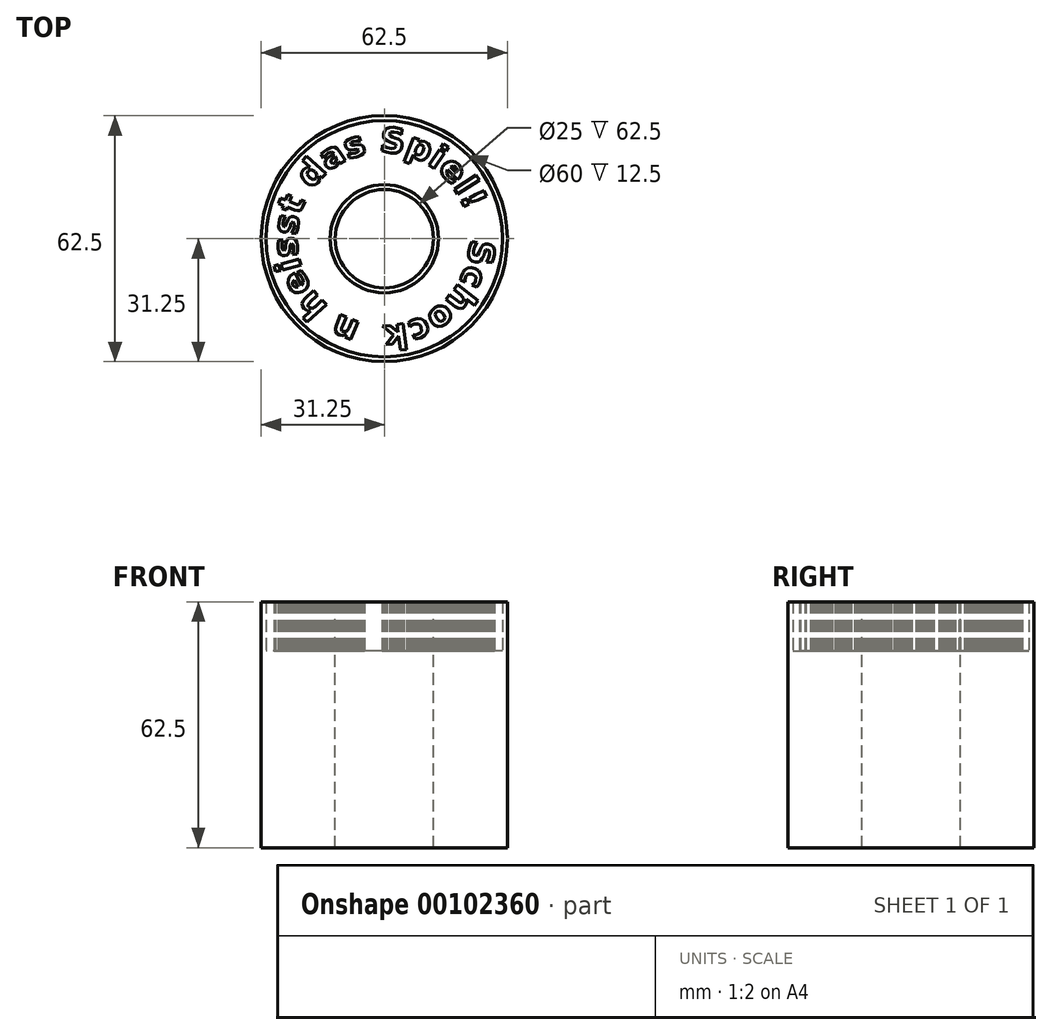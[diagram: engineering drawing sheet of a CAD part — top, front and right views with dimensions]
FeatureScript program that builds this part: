
annotation { "Feature Type Name" : "Feature", "Feature Type Description" : "" }
export const myFeature = defineFeature(function(context is Context, id is Id, definition is map)
    precondition{}
    {
        {
            var Q0;
            Q0=qCreatedBy(makeId("Top.planeOp"),FACE);
            var sketch = newSketch(context, id + "F0", { "sketchPlane" : qUnion([Q0])});
            skLineSegment(sketch, "E0", {"start": v(0.87, 0) * mm, "end": v(0.85, -0.18) * mm});
            skLineSegment(sketch, "E1", {"start": v(0.85, -0.18) * mm, "end": v(0.8, -0.34) * mm});
            skLineSegment(sketch, "E2", {"start": v(0.8, -0.34) * mm, "end": v(0.72, -0.5) * mm});
            skLineSegment(sketch, "E3", {"start": v(0.72, -0.5) * mm, "end": v(0.61, -0.62) * mm});
            skLineSegment(sketch, "E4", {"start": v(0.61, -0.62) * mm, "end": v(0.48, -0.73) * mm});
            skLineSegment(sketch, "E5", {"start": v(0.48, -0.73) * mm, "end": v(0.33, -0.81) * mm});
            skLineSegment(sketch, "E6", {"start": v(0.33, -0.81) * mm, "end": v(0.17, -0.86) * mm});
            skLineSegment(sketch, "E7", {"start": v(0.17, -0.86) * mm, "end": v(0, -0.88) * mm});
            skLineSegment(sketch, "E8", {"start": v(0, -0.88) * mm, "end": v(-0.19, -0.86) * mm});
            skLineSegment(sketch, "E9", {"start": v(-0.19, -0.86) * mm, "end": v(-0.35, -0.81) * mm});
            skLineSegment(sketch, "E10", {"start": v(-0.35, -0.81) * mm, "end": v(-0.5, -0.73) * mm});
            skLineSegment(sketch, "E11", {"start": v(-0.5, -0.73) * mm, "end": v(-0.63, -0.62) * mm});
            skLineSegment(sketch, "E12", {"start": v(-0.63, -0.62) * mm, "end": v(-0.74, -0.5) * mm});
            skLineSegment(sketch, "E13", {"start": v(-0.74, -0.5) * mm, "end": v(-0.82, -0.34) * mm});
            skLineSegment(sketch, "E14", {"start": v(-0.82, -0.34) * mm, "end": v(-0.87, -0.18) * mm});
            skLineSegment(sketch, "E15", {"start": v(-0.87, -0.18) * mm, "end": v(-0.89, 0) * mm});
            skLineSegment(sketch, "E16", {"start": v(-0.89, 0) * mm, "end": v(-0.87, 0.18) * mm});
            skLineSegment(sketch, "E17", {"start": v(-0.87, 0.18) * mm, "end": v(-0.82, 0.34) * mm});
            skLineSegment(sketch, "E18", {"start": v(-0.82, 0.34) * mm, "end": v(-0.74, 0.5) * mm});
            skLineSegment(sketch, "E19", {"start": v(-0.74, 0.5) * mm, "end": v(-0.63, 0.62) * mm});
            skLineSegment(sketch, "E20", {"start": v(-0.63, 0.62) * mm, "end": v(-0.5, 0.73) * mm});
            skLineSegment(sketch, "E21", {"start": v(-0.5, 0.73) * mm, "end": v(-0.35, 0.8) * mm});
            skLineSegment(sketch, "E22", {"start": v(-0.35, 0.8) * mm, "end": v(-0.19, 0.86) * mm});
            skLineSegment(sketch, "E23", {"start": v(-0.19, 0.86) * mm, "end": v(0, 0.88) * mm});
            skLineSegment(sketch, "E24", {"start": v(0, 0.88) * mm, "end": v(0.17, 0.86) * mm});
            skLineSegment(sketch, "E25", {"start": v(0.17, 0.86) * mm, "end": v(0.33, 0.8) * mm});
            skLineSegment(sketch, "E26", {"start": v(0.33, 0.8) * mm, "end": v(0.48, 0.73) * mm});
            skLineSegment(sketch, "E27", {"start": v(0.48, 0.73) * mm, "end": v(0.61, 0.62) * mm});
            skLineSegment(sketch, "E28", {"start": v(0.61, 0.62) * mm, "end": v(0.72, 0.5) * mm});
            skLineSegment(sketch, "E29", {"start": v(0.72, 0.5) * mm, "end": v(0.8, 0.34) * mm});
            skLineSegment(sketch, "E30", {"start": v(0.8, 0.34) * mm, "end": v(0.85, 0.18) * mm});
            skLineSegment(sketch, "E31", {"start": v(0.85, 0.18) * mm, "end": v(0.87, 0) * mm});
            skLineSegment(sketch, "E32", {"start": v(1.1, -0.24) * mm, "end": v(1.04, -0.24) * mm});
            skLineSegment(sketch, "E33", {"start": v(1.04, -0.24) * mm, "end": v(1.06, -0.2) * mm});
            skLineSegment(sketch, "E34", {"start": v(1.06, -0.2) * mm, "end": v(1.07, -0.16) * mm});
            skLineSegment(sketch, "E35", {"start": v(1.07, -0.16) * mm, "end": v(1.07, -0.13) * mm});
            skLineSegment(sketch, "E36", {"start": v(1.07, -0.13) * mm, "end": v(1.05, -0.11) * mm});
            skLineSegment(sketch, "E37", {"start": v(1.05, -0.11) * mm, "end": v(1.03, -0.12) * mm});
            skLineSegment(sketch, "E38", {"start": v(1.03, -0.12) * mm, "end": v(1.02, -0.14) * mm});
            skLineSegment(sketch, "E39", {"start": v(1.02, -0.14) * mm, "end": v(1.01, -0.17) * mm});
            skLineSegment(sketch, "E40", {"start": v(1.01, -0.17) * mm, "end": v(1, -0.2) * mm});
            skLineSegment(sketch, "E41", {"start": v(1, -0.2) * mm, "end": v(0.98, -0.23) * mm});
            skLineSegment(sketch, "E42", {"start": v(0.98, -0.23) * mm, "end": v(0.95, -0.24) * mm});
            skLineSegment(sketch, "E43", {"start": v(0.95, -0.24) * mm, "end": v(0.93, -0.24) * mm});
            skLineSegment(sketch, "E44", {"start": v(0.93, -0.24) * mm, "end": v(0.89, -0.22) * mm});
            skLineSegment(sketch, "E45", {"start": v(0.89, -0.22) * mm, "end": v(0.87, -0.2) * mm});
            skLineSegment(sketch, "E46", {"start": v(0.87, -0.2) * mm, "end": v(0.86, -0.17) * mm});
            skLineSegment(sketch, "E47", {"start": v(0.86, -0.17) * mm, "end": v(0.86, -0.12) * mm});
            skLineSegment(sketch, "E48", {"start": v(0.86, -0.12) * mm, "end": v(0.87, -0.08) * mm});
            skLineSegment(sketch, "E49", {"start": v(0.87, -0.08) * mm, "end": v(0.89, -0.03) * mm});
            skLineSegment(sketch, "E50", {"start": v(0.89, -0.03) * mm, "end": v(0.94, -0.04) * mm});
            skLineSegment(sketch, "E51", {"start": v(0.94, -0.04) * mm, "end": v(0.92, -0.08) * mm});
            skLineSegment(sketch, "E52", {"start": v(0.92, -0.08) * mm, "end": v(0.9, -0.12) * mm});
            skLineSegment(sketch, "E53", {"start": v(0.9, -0.12) * mm, "end": v(0.9, -0.16) * mm});
            skLineSegment(sketch, "E54", {"start": v(0.9, -0.16) * mm, "end": v(0.93, -0.17) * mm});
            skLineSegment(sketch, "E55", {"start": v(0.93, -0.17) * mm, "end": v(0.95, -0.17) * mm});
            skLineSegment(sketch, "E56", {"start": v(0.95, -0.17) * mm, "end": v(0.96, -0.14) * mm});
            skLineSegment(sketch, "E57", {"start": v(0.96, -0.14) * mm, "end": v(0.97, -0.11) * mm});
            skLineSegment(sketch, "E58", {"start": v(0.97, -0.11) * mm, "end": v(0.99, -0.08) * mm});
            skLineSegment(sketch, "E59", {"start": v(0.99, -0.08) * mm, "end": v(1, -0.06) * mm});
            skLineSegment(sketch, "E60", {"start": v(1, -0.06) * mm, "end": v(1.03, -0.05) * mm});
            skLineSegment(sketch, "E61", {"start": v(1.03, -0.05) * mm, "end": v(1.05, -0.05) * mm});
            skLineSegment(sketch, "E62", {"start": v(1.05, -0.05) * mm, "end": v(1.09, -0.06) * mm});
            skLineSegment(sketch, "E63", {"start": v(1.09, -0.06) * mm, "end": v(1.1, -0.08) * mm});
            skLineSegment(sketch, "E64", {"start": v(1.1, -0.08) * mm, "end": v(1.12, -0.12) * mm});
            skLineSegment(sketch, "E65", {"start": v(1.12, -0.12) * mm, "end": v(1.12, -0.16) * mm});
            skLineSegment(sketch, "E66", {"start": v(1.12, -0.16) * mm, "end": v(1.1, -0.2) * mm});
            skLineSegment(sketch, "E67", {"start": v(1.1, -0.2) * mm, "end": v(1.1, -0.24) * mm});
            skLineSegment(sketch, "E68", {"start": v(0.94, -0.5) * mm, "end": v(0.9, -0.47) * mm});
            skLineSegment(sketch, "E69", {"start": v(0.9, -0.47) * mm, "end": v(0.91, -0.45) * mm});
            skLineSegment(sketch, "E70", {"start": v(0.91, -0.45) * mm, "end": v(0.93, -0.43) * mm});
            skLineSegment(sketch, "E71", {"start": v(0.93, -0.43) * mm, "end": v(0.93, -0.39) * mm});
            skLineSegment(sketch, "E72", {"start": v(0.93, -0.39) * mm, "end": v(0.9, -0.36) * mm});
            skLineSegment(sketch, "E73", {"start": v(0.9, -0.36) * mm, "end": v(0.85, -0.36) * mm});
            skLineSegment(sketch, "E74", {"start": v(0.85, -0.36) * mm, "end": v(0.84, -0.37) * mm});
            skLineSegment(sketch, "E75", {"start": v(0.84, -0.37) * mm, "end": v(0.82, -0.39) * mm});
            skLineSegment(sketch, "E76", {"start": v(0.82, -0.39) * mm, "end": v(0.82, -0.41) * mm});
            skLineSegment(sketch, "E77", {"start": v(0.82, -0.41) * mm, "end": v(0.82, -0.44) * mm});
            skLineSegment(sketch, "E78", {"start": v(0.82, -0.44) * mm, "end": v(0.77, -0.42) * mm});
            skLineSegment(sketch, "E79", {"start": v(0.77, -0.42) * mm, "end": v(0.78, -0.4) * mm});
            skLineSegment(sketch, "E80", {"start": v(0.78, -0.4) * mm, "end": v(0.79, -0.36) * mm});
            skLineSegment(sketch, "E81", {"start": v(0.79, -0.36) * mm, "end": v(0.81, -0.32) * mm});
            skLineSegment(sketch, "E82", {"start": v(0.81, -0.32) * mm, "end": v(0.84, -0.3) * mm});
            skLineSegment(sketch, "E83", {"start": v(0.84, -0.3) * mm, "end": v(0.88, -0.3) * mm});
            skLineSegment(sketch, "E84", {"start": v(0.88, -0.3) * mm, "end": v(0.92, -0.3) * mm});
            skLineSegment(sketch, "E85", {"start": v(0.92, -0.3) * mm, "end": v(0.96, -0.33) * mm});
            skLineSegment(sketch, "E86", {"start": v(0.96, -0.33) * mm, "end": v(0.98, -0.36) * mm});
            skLineSegment(sketch, "E87", {"start": v(0.98, -0.36) * mm, "end": v(0.98, -0.4) * mm});
            skLineSegment(sketch, "E88", {"start": v(0.98, -0.4) * mm, "end": v(0.97, -0.44) * mm});
            skLineSegment(sketch, "E89", {"start": v(0.97, -0.44) * mm, "end": v(0.96, -0.47) * mm});
            skLineSegment(sketch, "E90", {"start": v(0.96, -0.47) * mm, "end": v(0.94, -0.5) * mm});
            skLineSegment(sketch, "E91", {"start": v(0.72, -0.69) * mm, "end": v(0.63, -0.62) * mm});
            skLineSegment(sketch, "E92", {"start": v(0.63, -0.62) * mm, "end": v(0.66, -0.57) * mm});
            skLineSegment(sketch, "E93", {"start": v(0.66, -0.57) * mm, "end": v(0.68, -0.58) * mm});
            skLineSegment(sketch, "E94", {"start": v(0.68, -0.58) * mm, "end": v(0.73, -0.62) * mm});
            skLineSegment(sketch, "E95", {"start": v(0.73, -0.62) * mm, "end": v(0.76, -0.64) * mm});
            skLineSegment(sketch, "E96", {"start": v(0.76, -0.64) * mm, "end": v(0.77, -0.65) * mm});
            skLineSegment(sketch, "E97", {"start": v(0.77, -0.65) * mm, "end": v(0.79, -0.65) * mm});
            skLineSegment(sketch, "E98", {"start": v(0.79, -0.65) * mm, "end": v(0.8, -0.64) * mm});
            skLineSegment(sketch, "E99", {"start": v(0.8, -0.64) * mm, "end": v(0.8, -0.6) * mm});
            skLineSegment(sketch, "E100", {"start": v(0.8, -0.6) * mm, "end": v(0.78, -0.57) * mm});
            skLineSegment(sketch, "E101", {"start": v(0.78, -0.57) * mm, "end": v(0.7, -0.51) * mm});
            skLineSegment(sketch, "E102", {"start": v(0.7, -0.51) * mm, "end": v(0.74, -0.47) * mm});
            skLineSegment(sketch, "E103", {"start": v(0.74, -0.47) * mm, "end": v(0.95, -0.63) * mm});
            skLineSegment(sketch, "E104", {"start": v(0.95, -0.63) * mm, "end": v(0.91, -0.68) * mm});
            skLineSegment(sketch, "E105", {"start": v(0.91, -0.68) * mm, "end": v(0.83, -0.62) * mm});
            skLineSegment(sketch, "E106", {"start": v(0.83, -0.62) * mm, "end": v(0.84, -0.65) * mm});
            skLineSegment(sketch, "E107", {"start": v(0.84, -0.65) * mm, "end": v(0.82, -0.69) * mm});
            skLineSegment(sketch, "E108", {"start": v(0.82, -0.69) * mm, "end": v(0.8, -0.7) * mm});
            skLineSegment(sketch, "E109", {"start": v(0.8, -0.7) * mm, "end": v(0.77, -0.71) * mm});
            skLineSegment(sketch, "E110", {"start": v(0.77, -0.71) * mm, "end": v(0.75, -0.7) * mm});
            skLineSegment(sketch, "E111", {"start": v(0.75, -0.7) * mm, "end": v(0.72, -0.69) * mm});
            skLineSegment(sketch, "E112", {"start": v(0.6, -0.83) * mm, "end": v(0.62, -0.8) * mm});
            skLineSegment(sketch, "E113", {"start": v(0.62, -0.8) * mm, "end": v(0.6, -0.76) * mm});
            skLineSegment(sketch, "E114", {"start": v(0.6, -0.76) * mm, "end": v(0.57, -0.74) * mm});
            skLineSegment(sketch, "E115", {"start": v(0.57, -0.74) * mm, "end": v(0.53, -0.74) * mm});
            skLineSegment(sketch, "E116", {"start": v(0.53, -0.74) * mm, "end": v(0.52, -0.77) * mm});
            skLineSegment(sketch, "E117", {"start": v(0.52, -0.77) * mm, "end": v(0.53, -0.81) * mm});
            skLineSegment(sketch, "E118", {"start": v(0.53, -0.81) * mm, "end": v(0.57, -0.84) * mm});
            skLineSegment(sketch, "E119", {"start": v(0.57, -0.84) * mm, "end": v(0.6, -0.83) * mm});
            skLineSegment(sketch, "E120", {"start": v(0.63, -0.87) * mm, "end": v(0.59, -0.89) * mm});
            skLineSegment(sketch, "E121", {"start": v(0.59, -0.89) * mm, "end": v(0.55, -0.9) * mm});
            skLineSegment(sketch, "E122", {"start": v(0.55, -0.9) * mm, "end": v(0.51, -0.88) * mm});
            skLineSegment(sketch, "E123", {"start": v(0.51, -0.88) * mm, "end": v(0.48, -0.85) * mm});
            skLineSegment(sketch, "E124", {"start": v(0.48, -0.85) * mm, "end": v(0.46, -0.81) * mm});
            skLineSegment(sketch, "E125", {"start": v(0.46, -0.81) * mm, "end": v(0.46, -0.77) * mm});
            skLineSegment(sketch, "E126", {"start": v(0.46, -0.77) * mm, "end": v(0.48, -0.74) * mm});
            skLineSegment(sketch, "E127", {"start": v(0.48, -0.74) * mm, "end": v(0.5, -0.7) * mm});
            skLineSegment(sketch, "E128", {"start": v(0.5, -0.7) * mm, "end": v(0.55, -0.69) * mm});
            skLineSegment(sketch, "E129", {"start": v(0.55, -0.69) * mm, "end": v(0.59, -0.68) * mm});
            skLineSegment(sketch, "E130", {"start": v(0.59, -0.68) * mm, "end": v(0.62, -0.7) * mm});
            skLineSegment(sketch, "E131", {"start": v(0.62, -0.7) * mm, "end": v(0.65, -0.73) * mm});
            skLineSegment(sketch, "E132", {"start": v(0.65, -0.73) * mm, "end": v(0.67, -0.76) * mm});
            skLineSegment(sketch, "E133", {"start": v(0.67, -0.76) * mm, "end": v(0.67, -0.8) * mm});
            skLineSegment(sketch, "E134", {"start": v(0.67, -0.8) * mm, "end": v(0.66, -0.84) * mm});
            skLineSegment(sketch, "E135", {"start": v(0.66, -0.84) * mm, "end": v(0.63, -0.87) * mm});
            skLineSegment(sketch, "E136", {"start": v(0.3, -1.02) * mm, "end": v(0.3, -0.97) * mm});
            skLineSegment(sketch, "E137", {"start": v(0.3, -0.97) * mm, "end": v(0.32, -0.98) * mm});
            skLineSegment(sketch, "E138", {"start": v(0.32, -0.98) * mm, "end": v(0.34, -0.97) * mm});
            skLineSegment(sketch, "E139", {"start": v(0.34, -0.97) * mm, "end": v(0.36, -0.96) * mm});
            skLineSegment(sketch, "E140", {"start": v(0.36, -0.96) * mm, "end": v(0.38, -0.94) * mm});
            skLineSegment(sketch, "E141", {"start": v(0.38, -0.94) * mm, "end": v(0.37, -0.9) * mm});
            skLineSegment(sketch, "E142", {"start": v(0.37, -0.9) * mm, "end": v(0.36, -0.88) * mm});
            skLineSegment(sketch, "E143", {"start": v(0.36, -0.88) * mm, "end": v(0.35, -0.86) * mm});
            skLineSegment(sketch, "E144", {"start": v(0.35, -0.86) * mm, "end": v(0.3, -0.87) * mm});
            skLineSegment(sketch, "E145", {"start": v(0.3, -0.87) * mm, "end": v(0.28, -0.88) * mm});
            skLineSegment(sketch, "E146", {"start": v(0.28, -0.88) * mm, "end": v(0.26, -0.9) * mm});
            skLineSegment(sketch, "E147", {"start": v(0.26, -0.9) * mm, "end": v(0.24, -0.85) * mm});
            skLineSegment(sketch, "E148", {"start": v(0.24, -0.85) * mm, "end": v(0.27, -0.84) * mm});
            skLineSegment(sketch, "E149", {"start": v(0.27, -0.84) * mm, "end": v(0.3, -0.82) * mm});
            skLineSegment(sketch, "E150", {"start": v(0.3, -0.82) * mm, "end": v(0.34, -0.81) * mm});
            skLineSegment(sketch, "E151", {"start": v(0.34, -0.81) * mm, "end": v(0.38, -0.82) * mm});
            skLineSegment(sketch, "E152", {"start": v(0.38, -0.82) * mm, "end": v(0.41, -0.84) * mm});
            skLineSegment(sketch, "E153", {"start": v(0.41, -0.84) * mm, "end": v(0.43, -0.87) * mm});
            skLineSegment(sketch, "E154", {"start": v(0.43, -0.87) * mm, "end": v(0.44, -0.92) * mm});
            skLineSegment(sketch, "E155", {"start": v(0.44, -0.92) * mm, "end": v(0.43, -0.95) * mm});
            skLineSegment(sketch, "E156", {"start": v(0.43, -0.95) * mm, "end": v(0.4, -0.99) * mm});
            skLineSegment(sketch, "E157", {"start": v(0.4, -0.99) * mm, "end": v(0.37, -1) * mm});
            skLineSegment(sketch, "E158", {"start": v(0.37, -1) * mm, "end": v(0.34, -1.02) * mm});
            skLineSegment(sketch, "E159", {"start": v(0.34, -1.02) * mm, "end": v(0.3, -1.02) * mm});
            skLineSegment(sketch, "E160", {"start": v(0.22, -1.12) * mm, "end": v(0.16, -1.13) * mm});
            skLineSegment(sketch, "E161", {"start": v(0.16, -1.13) * mm, "end": v(0.15, -0.99) * mm});
            skLineSegment(sketch, "E162", {"start": v(0.15, -0.99) * mm, "end": v(0.09, -1.07) * mm});
            skLineSegment(sketch, "E163", {"start": v(0.09, -1.07) * mm, "end": v(0.02, -1.08) * mm});
            skLineSegment(sketch, "E164", {"start": v(0.02, -1.08) * mm, "end": v(0.1, -0.98) * mm});
            skLineSegment(sketch, "E165", {"start": v(0.1, -0.98) * mm, "end": v(-0.02, -0.89) * mm});
            skLineSegment(sketch, "E166", {"start": v(-0.02, -0.89) * mm, "end": v(0.06, -0.88) * mm});
            skLineSegment(sketch, "E167", {"start": v(0.06, -0.88) * mm, "end": v(0.14, -0.95) * mm});
            skLineSegment(sketch, "E168", {"start": v(0.14, -0.95) * mm, "end": v(0.13, -0.87) * mm});
            skLineSegment(sketch, "E169", {"start": v(0.13, -0.87) * mm, "end": v(0.19, -0.86) * mm});
            skLineSegment(sketch, "E170", {"start": v(0.19, -0.86) * mm, "end": v(0.22, -1.12) * mm});
            skLineSegment(sketch, "E171", {"start": v(-0.23, -0.96) * mm, "end": v(-0.23, -0.94) * mm});
            skLineSegment(sketch, "E172", {"start": v(-0.23, -0.94) * mm, "end": v(-0.09, -0.96) * mm});
            skLineSegment(sketch, "E173", {"start": v(-0.09, -0.96) * mm, "end": v(-0.1, -0.92) * mm});
            skLineSegment(sketch, "E174", {"start": v(-0.1, -0.92) * mm, "end": v(-0.14, -0.9) * mm});
            skLineSegment(sketch, "E175", {"start": v(-0.14, -0.9) * mm, "end": v(-0.18, -0.9) * mm});
            skLineSegment(sketch, "E176", {"start": v(-0.18, -0.9) * mm, "end": v(-0.22, -0.92) * mm});
            skLineSegment(sketch, "E177", {"start": v(-0.22, -0.92) * mm, "end": v(-0.21, -0.87) * mm});
            skLineSegment(sketch, "E178", {"start": v(-0.21, -0.87) * mm, "end": v(-0.17, -0.87) * mm});
            skLineSegment(sketch, "E179", {"start": v(-0.17, -0.87) * mm, "end": v(-0.13, -0.87) * mm});
            skLineSegment(sketch, "E180", {"start": v(-0.13, -0.87) * mm, "end": v(-0.08, -0.88) * mm});
            skLineSegment(sketch, "E181", {"start": v(-0.08, -0.88) * mm, "end": v(-0.05, -0.9) * mm});
            skLineSegment(sketch, "E182", {"start": v(-0.05, -0.9) * mm, "end": v(-0.03, -0.94) * mm});
            skLineSegment(sketch, "E183", {"start": v(-0.03, -0.94) * mm, "end": v(-0.03, -0.98) * mm});
            skLineSegment(sketch, "E184", {"start": v(-0.03, -0.98) * mm, "end": v(-0.04, -1.02) * mm});
            skLineSegment(sketch, "E185", {"start": v(-0.04, -1.02) * mm, "end": v(-0.07, -1.05) * mm});
            skLineSegment(sketch, "E186", {"start": v(-0.07, -1.05) * mm, "end": v(-0.1, -1.07) * mm});
            skLineSegment(sketch, "E187", {"start": v(-0.1, -1.07) * mm, "end": v(-0.15, -1.07) * mm});
            skLineSegment(sketch, "E188", {"start": v(-0.15, -1.07) * mm, "end": v(-0.19, -1.06) * mm});
            skLineSegment(sketch, "E189", {"start": v(-0.19, -1.06) * mm, "end": v(-0.22, -1.03) * mm});
            skLineSegment(sketch, "E190", {"start": v(-0.14, -1) * mm, "end": v(-0.15, -0.96) * mm});
            skLineSegment(sketch, "E191", {"start": v(-0.23, -1) * mm, "end": v(-0.23, -0.96) * mm});
            skLineSegment(sketch, "E192", {"start": v(-0.17, -0.98) * mm, "end": v(-0.17, -1.01) * mm});
            skLineSegment(sketch, "E193", {"start": v(-0.17, -1.01) * mm, "end": v(-0.14, -1.03) * mm});
            skLineSegment(sketch, "E194", {"start": v(-0.14, -1.03) * mm, "end": v(-0.11, -1.02) * mm});
            skLineSegment(sketch, "E195", {"start": v(-0.11, -1.02) * mm, "end": v(-0.1, -1) * mm});
            skLineSegment(sketch, "E196", {"start": v(-0.1, -1) * mm, "end": v(-0.17, -0.98) * mm});
            skLineSegment(sketch, "E197", {"start": v(-0.49, -0.88) * mm, "end": v(-0.44, -0.77) * mm});
            skLineSegment(sketch, "E198", {"start": v(-0.44, -0.77) * mm, "end": v(-0.39, -0.8) * mm});
            skLineSegment(sketch, "E199", {"start": v(-0.39, -0.8) * mm, "end": v(-0.4, -0.81) * mm});
            skLineSegment(sketch, "E200", {"start": v(-0.4, -0.81) * mm, "end": v(-0.42, -0.88) * mm});
            skLineSegment(sketch, "E201", {"start": v(-0.42, -0.88) * mm, "end": v(-0.43, -0.91) * mm});
            skLineSegment(sketch, "E202", {"start": v(-0.43, -0.91) * mm, "end": v(-0.43, -0.92) * mm});
            skLineSegment(sketch, "E203", {"start": v(-0.43, -0.92) * mm, "end": v(-0.43, -0.94) * mm});
            skLineSegment(sketch, "E204", {"start": v(-0.43, -0.94) * mm, "end": v(-0.42, -0.95) * mm});
            skLineSegment(sketch, "E205", {"start": v(-0.42, -0.95) * mm, "end": v(-0.38, -0.94) * mm});
            skLineSegment(sketch, "E206", {"start": v(-0.38, -0.94) * mm, "end": v(-0.36, -0.91) * mm});
            skLineSegment(sketch, "E207", {"start": v(-0.36, -0.91) * mm, "end": v(-0.32, -0.82) * mm});
            skLineSegment(sketch, "E208", {"start": v(-0.32, -0.82) * mm, "end": v(-0.27, -0.85) * mm});
            skLineSegment(sketch, "E209", {"start": v(-0.27, -0.85) * mm, "end": v(-0.34, -1.02) * mm});
            skLineSegment(sketch, "E210", {"start": v(-0.34, -1.02) * mm, "end": v(-0.4, -1) * mm});
            skLineSegment(sketch, "E211", {"start": v(-0.4, -1) * mm, "end": v(-0.39, -0.97) * mm});
            skLineSegment(sketch, "E212", {"start": v(-0.39, -0.97) * mm, "end": v(-0.42, -0.98) * mm});
            skLineSegment(sketch, "E213", {"start": v(-0.42, -0.98) * mm, "end": v(-0.46, -0.98) * mm});
            skLineSegment(sketch, "E214", {"start": v(-0.46, -0.98) * mm, "end": v(-0.48, -0.96) * mm});
            skLineSegment(sketch, "E215", {"start": v(-0.48, -0.96) * mm, "end": v(-0.5, -0.94) * mm});
            skLineSegment(sketch, "E216", {"start": v(-0.5, -0.94) * mm, "end": v(-0.5, -0.91) * mm});
            skLineSegment(sketch, "E217", {"start": v(-0.5, -0.91) * mm, "end": v(-0.49, -0.88) * mm});
            skLineSegment(sketch, "E218", {"start": v(-0.8, -0.6) * mm, "end": v(-0.72, -0.53) * mm});
            skLineSegment(sketch, "E219", {"start": v(-0.72, -0.53) * mm, "end": v(-0.68, -0.57) * mm});
            skLineSegment(sketch, "E220", {"start": v(-0.68, -0.57) * mm, "end": v(-0.7, -0.59) * mm});
            skLineSegment(sketch, "E221", {"start": v(-0.7, -0.59) * mm, "end": v(-0.74, -0.63) * mm});
            skLineSegment(sketch, "E222", {"start": v(-0.74, -0.63) * mm, "end": v(-0.77, -0.66) * mm});
            skLineSegment(sketch, "E223", {"start": v(-0.77, -0.66) * mm, "end": v(-0.77, -0.67) * mm});
            skLineSegment(sketch, "E224", {"start": v(-0.77, -0.67) * mm, "end": v(-0.77, -0.68) * mm});
            skLineSegment(sketch, "E225", {"start": v(-0.77, -0.68) * mm, "end": v(-0.77, -0.7) * mm});
            skLineSegment(sketch, "E226", {"start": v(-0.77, -0.7) * mm, "end": v(-0.74, -0.7) * mm});
            skLineSegment(sketch, "E227", {"start": v(-0.74, -0.7) * mm, "end": v(-0.7, -0.69) * mm});
            skLineSegment(sketch, "E228", {"start": v(-0.7, -0.69) * mm, "end": v(-0.63, -0.62) * mm});
            skLineSegment(sketch, "E229", {"start": v(-0.63, -0.62) * mm, "end": v(-0.59, -0.67) * mm});
            skLineSegment(sketch, "E230", {"start": v(-0.59, -0.67) * mm, "end": v(-0.78, -0.85) * mm});
            skLineSegment(sketch, "E231", {"start": v(-0.78, -0.85) * mm, "end": v(-0.82, -0.8) * mm});
            skLineSegment(sketch, "E232", {"start": v(-0.82, -0.8) * mm, "end": v(-0.75, -0.73) * mm});
            skLineSegment(sketch, "E233", {"start": v(-0.75, -0.73) * mm, "end": v(-0.79, -0.73) * mm});
            skLineSegment(sketch, "E234", {"start": v(-0.79, -0.73) * mm, "end": v(-0.82, -0.71) * mm});
            skLineSegment(sketch, "E235", {"start": v(-0.82, -0.71) * mm, "end": v(-0.83, -0.69) * mm});
            skLineSegment(sketch, "E236", {"start": v(-0.83, -0.69) * mm, "end": v(-0.84, -0.66) * mm});
            skLineSegment(sketch, "E237", {"start": v(-0.84, -0.66) * mm, "end": v(-0.83, -0.63) * mm});
            skLineSegment(sketch, "E238", {"start": v(-0.83, -0.63) * mm, "end": v(-0.8, -0.6) * mm});
            skLineSegment(sketch, "E239", {"start": v(-0.92, -0.35) * mm, "end": v(-0.9, -0.35) * mm});
            skLineSegment(sketch, "E240", {"start": v(-0.9, -0.35) * mm, "end": v(-0.84, -0.47) * mm});
            skLineSegment(sketch, "E241", {"start": v(-0.84, -0.47) * mm, "end": v(-0.82, -0.45) * mm});
            skLineSegment(sketch, "E242", {"start": v(-0.82, -0.45) * mm, "end": v(-0.83, -0.4) * mm});
            skLineSegment(sketch, "E243", {"start": v(-0.83, -0.4) * mm, "end": v(-0.85, -0.37) * mm});
            skLineSegment(sketch, "E244", {"start": v(-0.85, -0.37) * mm, "end": v(-0.89, -0.35) * mm});
            skLineSegment(sketch, "E245", {"start": v(-0.89, -0.35) * mm, "end": v(-0.84, -0.32) * mm});
            skLineSegment(sketch, "E246", {"start": v(-0.84, -0.32) * mm, "end": v(-0.81, -0.36) * mm});
            skLineSegment(sketch, "E247", {"start": v(-0.81, -0.36) * mm, "end": v(-0.8, -0.4) * mm});
            skLineSegment(sketch, "E248", {"start": v(-0.8, -0.4) * mm, "end": v(-0.78, -0.44) * mm});
            skLineSegment(sketch, "E249", {"start": v(-0.78, -0.44) * mm, "end": v(-0.78, -0.48) * mm});
            skLineSegment(sketch, "E250", {"start": v(-0.78, -0.48) * mm, "end": v(-0.8, -0.51) * mm});
            skLineSegment(sketch, "E251", {"start": v(-0.8, -0.51) * mm, "end": v(-0.83, -0.54) * mm});
            skLineSegment(sketch, "E252", {"start": v(-0.83, -0.54) * mm, "end": v(-0.87, -0.55) * mm});
            skLineSegment(sketch, "E253", {"start": v(-0.87, -0.55) * mm, "end": v(-0.9, -0.55) * mm});
            skLineSegment(sketch, "E254", {"start": v(-0.9, -0.55) * mm, "end": v(-0.94, -0.52) * mm});
            skLineSegment(sketch, "E255", {"start": v(-0.94, -0.52) * mm, "end": v(-0.97, -0.49) * mm});
            skLineSegment(sketch, "E256", {"start": v(-0.97, -0.49) * mm, "end": v(-0.98, -0.45) * mm});
            skLineSegment(sketch, "E257", {"start": v(-0.98, -0.45) * mm, "end": v(-0.98, -0.41) * mm});
            skLineSegment(sketch, "E258", {"start": v(-0.98, -0.41) * mm, "end": v(-0.96, -0.38) * mm});
            skLineSegment(sketch, "E259", {"start": v(-0.96, -0.38) * mm, "end": v(-0.92, -0.35) * mm});
            skLineSegment(sketch, "E260", {"start": v(-0.91, -0.42) * mm, "end": v(-0.93, -0.44) * mm});
            skLineSegment(sketch, "E261", {"start": v(-0.93, -0.44) * mm, "end": v(-0.93, -0.47) * mm});
            skLineSegment(sketch, "E262", {"start": v(-0.93, -0.47) * mm, "end": v(-0.9, -0.5) * mm});
            skLineSegment(sketch, "E263", {"start": v(-0.9, -0.5) * mm, "end": v(-0.88, -0.5) * mm});
            skLineSegment(sketch, "E264", {"start": v(-0.88, -0.5) * mm, "end": v(-0.91, -0.42) * mm});
            skLineSegment(sketch, "E265", {"start": v(-1.03, -0.32) * mm, "end": v(-1.05, -0.26) * mm});
            skLineSegment(sketch, "E266", {"start": v(-1.05, -0.26) * mm, "end": v(-0.86, -0.2) * mm});
            skLineSegment(sketch, "E267", {"start": v(-0.86, -0.2) * mm, "end": v(-0.85, -0.27) * mm});
            skLineSegment(sketch, "E268", {"start": v(-0.85, -0.27) * mm, "end": v(-1.03, -0.32) * mm});
            skLineSegment(sketch, "E269", {"start": v(-1.1, -0.34) * mm, "end": v(-1.12, -0.28) * mm});
            skLineSegment(sketch, "E270", {"start": v(-1.12, -0.28) * mm, "end": v(-1.07, -0.26) * mm});
            skLineSegment(sketch, "E271", {"start": v(-1.07, -0.26) * mm, "end": v(-1.06, -0.32) * mm});
            skLineSegment(sketch, "E272", {"start": v(-1.06, -0.32) * mm, "end": v(-1.1, -0.34) * mm});
            skLineSegment(sketch, "E273", {"start": v(-1.08, -0.02) * mm, "end": v(-1.03, -0.01) * mm});
            skLineSegment(sketch, "E274", {"start": v(-1.03, -0.01) * mm, "end": v(-1.04, -0.05) * mm});
            skLineSegment(sketch, "E275", {"start": v(-1.04, -0.05) * mm, "end": v(-1.04, -0.09) * mm});
            skLineSegment(sketch, "E276", {"start": v(-1.04, -0.09) * mm, "end": v(-1.03, -0.11) * mm});
            skLineSegment(sketch, "E277", {"start": v(-1.03, -0.11) * mm, "end": v(-1.02, -0.12) * mm});
            skLineSegment(sketch, "E278", {"start": v(-1.02, -0.12) * mm, "end": v(-1, -0.11) * mm});
            skLineSegment(sketch, "E279", {"start": v(-1, -0.11) * mm, "end": v(-1, -0.09) * mm});
            skLineSegment(sketch, "E280", {"start": v(-1, -0.09) * mm, "end": v(-1, -0.08) * mm});
            skLineSegment(sketch, "E281", {"start": v(-1, -0.08) * mm, "end": v(-1, -0.04) * mm});
            skLineSegment(sketch, "E282", {"start": v(-1, -0.04) * mm, "end": v(-0.99, -0.01) * mm});
            skLineSegment(sketch, "E283", {"start": v(-0.99, -0.01) * mm, "end": v(-0.97, 0) * mm});
            skLineSegment(sketch, "E284", {"start": v(-0.97, 0) * mm, "end": v(-0.95, 0) * mm});
            skLineSegment(sketch, "E285", {"start": v(-0.95, 0) * mm, "end": v(-0.92, 0) * mm});
            skLineSegment(sketch, "E286", {"start": v(-0.92, 0) * mm, "end": v(-0.9, -0.01) * mm});
            skLineSegment(sketch, "E287", {"start": v(-0.9, -0.01) * mm, "end": v(-0.89, -0.04) * mm});
            skLineSegment(sketch, "E288", {"start": v(-0.89, -0.04) * mm, "end": v(-0.88, -0.08) * mm});
            skLineSegment(sketch, "E289", {"start": v(-0.88, -0.08) * mm, "end": v(-0.88, -0.12) * mm});
            skLineSegment(sketch, "E290", {"start": v(-0.88, -0.12) * mm, "end": v(-0.89, -0.16) * mm});
            skLineSegment(sketch, "E291", {"start": v(-0.89, -0.16) * mm, "end": v(-0.93, -0.16) * mm});
            skLineSegment(sketch, "E292", {"start": v(-0.93, -0.16) * mm, "end": v(-0.92, -0.12) * mm});
            skLineSegment(sketch, "E293", {"start": v(-0.92, -0.12) * mm, "end": v(-0.92, -0.08) * mm});
            skLineSegment(sketch, "E294", {"start": v(-0.92, -0.08) * mm, "end": v(-0.93, -0.06) * mm});
            skLineSegment(sketch, "E295", {"start": v(-0.93, -0.06) * mm, "end": v(-0.94, -0.05) * mm});
            skLineSegment(sketch, "E296", {"start": v(-0.94, -0.05) * mm, "end": v(-0.95, -0.06) * mm});
            skLineSegment(sketch, "E297", {"start": v(-0.95, -0.06) * mm, "end": v(-0.96, -0.08) * mm});
            skLineSegment(sketch, "E298", {"start": v(-0.96, -0.08) * mm, "end": v(-0.96, -0.1) * mm});
            skLineSegment(sketch, "E299", {"start": v(-0.96, -0.1) * mm, "end": v(-0.96, -0.13) * mm});
            skLineSegment(sketch, "E300", {"start": v(-0.96, -0.13) * mm, "end": v(-0.97, -0.15) * mm});
            skLineSegment(sketch, "E301", {"start": v(-0.97, -0.15) * mm, "end": v(-0.99, -0.17) * mm});
            skLineSegment(sketch, "E302", {"start": v(-0.99, -0.17) * mm, "end": v(-1.01, -0.17) * mm});
            skLineSegment(sketch, "E303", {"start": v(-1.01, -0.17) * mm, "end": v(-1.04, -0.17) * mm});
            skLineSegment(sketch, "E304", {"start": v(-1.04, -0.17) * mm, "end": v(-1.06, -0.15) * mm});
            skLineSegment(sketch, "E305", {"start": v(-1.06, -0.15) * mm, "end": v(-1.07, -0.13) * mm});
            skLineSegment(sketch, "E306", {"start": v(-1.07, -0.13) * mm, "end": v(-1.08, -0.1) * mm});
            skLineSegment(sketch, "E307", {"start": v(-1.08, -0.1) * mm, "end": v(-1.08, -0.06) * mm});
            skLineSegment(sketch, "E308", {"start": v(-1.08, -0.06) * mm, "end": v(-1.08, -0.02) * mm});
            skLineSegment(sketch, "E309", {"start": v(-1.05, 0.23) * mm, "end": v(-1, 0.23) * mm});
            skLineSegment(sketch, "E310", {"start": v(-1, 0.23) * mm, "end": v(-1.02, 0.2) * mm});
            skLineSegment(sketch, "E311", {"start": v(-1.02, 0.2) * mm, "end": v(-1.03, 0.16) * mm});
            skLineSegment(sketch, "E312", {"start": v(-1.03, 0.16) * mm, "end": v(-1.03, 0.13) * mm});
            skLineSegment(sketch, "E313", {"start": v(-1.03, 0.13) * mm, "end": v(-1.02, 0.12) * mm});
            skLineSegment(sketch, "E314", {"start": v(-1.02, 0.12) * mm, "end": v(-1, 0.13) * mm});
            skLineSegment(sketch, "E315", {"start": v(-1, 0.13) * mm, "end": v(-1, 0.15) * mm});
            skLineSegment(sketch, "E316", {"start": v(-1, 0.15) * mm, "end": v(-1, 0.16) * mm});
            skLineSegment(sketch, "E317", {"start": v(-1, 0.16) * mm, "end": v(-0.98, 0.2) * mm});
            skLineSegment(sketch, "E318", {"start": v(-0.98, 0.2) * mm, "end": v(-0.97, 0.22) * mm});
            skLineSegment(sketch, "E319", {"start": v(-0.97, 0.22) * mm, "end": v(-0.95, 0.23) * mm});
            skLineSegment(sketch, "E320", {"start": v(-0.95, 0.23) * mm, "end": v(-0.92, 0.23) * mm});
            skLineSegment(sketch, "E321", {"start": v(-0.92, 0.23) * mm, "end": v(-0.9, 0.22) * mm});
            skLineSegment(sketch, "E322", {"start": v(-0.9, 0.22) * mm, "end": v(-0.88, 0.2) * mm});
            skLineSegment(sketch, "E323", {"start": v(-0.88, 0.2) * mm, "end": v(-0.87, 0.17) * mm});
            skLineSegment(sketch, "E324", {"start": v(-0.87, 0.17) * mm, "end": v(-0.87, 0.13) * mm});
            skLineSegment(sketch, "E325", {"start": v(-0.87, 0.13) * mm, "end": v(-0.88, 0.1) * mm});
            skLineSegment(sketch, "E326", {"start": v(-0.88, 0.1) * mm, "end": v(-0.9, 0.05) * mm});
            skLineSegment(sketch, "E327", {"start": v(-0.9, 0.05) * mm, "end": v(-0.94, 0.06) * mm});
            skLineSegment(sketch, "E328", {"start": v(-0.94, 0.06) * mm, "end": v(-0.92, 0.1) * mm});
            skLineSegment(sketch, "E329", {"start": v(-0.92, 0.1) * mm, "end": v(-0.91, 0.13) * mm});
            skLineSegment(sketch, "E330", {"start": v(-0.91, 0.13) * mm, "end": v(-0.92, 0.16) * mm});
            skLineSegment(sketch, "E331", {"start": v(-0.92, 0.16) * mm, "end": v(-0.93, 0.17) * mm});
            skLineSegment(sketch, "E332", {"start": v(-0.93, 0.17) * mm, "end": v(-0.94, 0.16) * mm});
            skLineSegment(sketch, "E333", {"start": v(-0.94, 0.16) * mm, "end": v(-0.95, 0.14) * mm});
            skLineSegment(sketch, "E334", {"start": v(-0.95, 0.14) * mm, "end": v(-0.95, 0.13) * mm});
            skLineSegment(sketch, "E335", {"start": v(-0.95, 0.13) * mm, "end": v(-0.97, 0.1) * mm});
            skLineSegment(sketch, "E336", {"start": v(-0.97, 0.1) * mm, "end": v(-0.98, 0.08) * mm});
            skLineSegment(sketch, "E337", {"start": v(-0.98, 0.08) * mm, "end": v(-1, 0.07) * mm});
            skLineSegment(sketch, "E338", {"start": v(-1, 0.07) * mm, "end": v(-1.03, 0.07) * mm});
            skLineSegment(sketch, "E339", {"start": v(-1.03, 0.07) * mm, "end": v(-1.05, 0.08) * mm});
            skLineSegment(sketch, "E340", {"start": v(-1.05, 0.08) * mm, "end": v(-1.07, 0.1) * mm});
            skLineSegment(sketch, "E341", {"start": v(-1.07, 0.1) * mm, "end": v(-1.07, 0.12) * mm});
            skLineSegment(sketch, "E342", {"start": v(-1.07, 0.12) * mm, "end": v(-1.07, 0.16) * mm});
            skLineSegment(sketch, "E343", {"start": v(-1.07, 0.16) * mm, "end": v(-1.06, 0.2) * mm});
            skLineSegment(sketch, "E344", {"start": v(-1.06, 0.2) * mm, "end": v(-1.05, 0.23) * mm});
            skLineSegment(sketch, "E345", {"start": v(-1.05, 0.41) * mm, "end": v(-1, 0.4) * mm});
            skLineSegment(sketch, "E346", {"start": v(-1, 0.4) * mm, "end": v(-0.98, 0.45) * mm});
            skLineSegment(sketch, "E347", {"start": v(-0.98, 0.45) * mm, "end": v(-0.94, 0.44) * mm});
            skLineSegment(sketch, "E348", {"start": v(-0.94, 0.44) * mm, "end": v(-0.96, 0.38) * mm});
            skLineSegment(sketch, "E349", {"start": v(-0.96, 0.38) * mm, "end": v(-0.89, 0.35) * mm});
            skLineSegment(sketch, "E350", {"start": v(-0.89, 0.35) * mm, "end": v(-0.87, 0.35) * mm});
            skLineSegment(sketch, "E351", {"start": v(-0.87, 0.35) * mm, "end": v(-0.86, 0.36) * mm});
            skLineSegment(sketch, "E352", {"start": v(-0.86, 0.36) * mm, "end": v(-0.85, 0.4) * mm});
            skLineSegment(sketch, "E353", {"start": v(-0.85, 0.4) * mm, "end": v(-0.8, 0.38) * mm});
            skLineSegment(sketch, "E354", {"start": v(-0.8, 0.38) * mm, "end": v(-0.82, 0.33) * mm});
            skLineSegment(sketch, "E355", {"start": v(-0.82, 0.33) * mm, "end": v(-0.84, 0.3) * mm});
            skLineSegment(sketch, "E356", {"start": v(-0.84, 0.3) * mm, "end": v(-0.86, 0.29) * mm});
            skLineSegment(sketch, "E357", {"start": v(-0.86, 0.29) * mm, "end": v(-0.88, 0.28) * mm});
            skLineSegment(sketch, "E358", {"start": v(-0.88, 0.28) * mm, "end": v(-0.9, 0.3) * mm});
            skLineSegment(sketch, "E359", {"start": v(-0.9, 0.3) * mm, "end": v(-0.99, 0.32) * mm});
            skLineSegment(sketch, "E360", {"start": v(-0.99, 0.32) * mm, "end": v(-1, 0.3) * mm});
            skLineSegment(sketch, "E361", {"start": v(-1, 0.3) * mm, "end": v(-1.04, 0.3) * mm});
            skLineSegment(sketch, "E362", {"start": v(-1.04, 0.3) * mm, "end": v(-1.03, 0.34) * mm});
            skLineSegment(sketch, "E363", {"start": v(-1.03, 0.34) * mm, "end": v(-1.08, 0.35) * mm});
            skLineSegment(sketch, "E364", {"start": v(-1.08, 0.35) * mm, "end": v(-1.05, 0.41) * mm});
            skLineSegment(sketch, "E365", {"start": v(-0.76, 0.73) * mm, "end": v(-0.83, 0.8) * mm});
            skLineSegment(sketch, "E366", {"start": v(-0.83, 0.8) * mm, "end": v(-0.79, 0.84) * mm});
            skLineSegment(sketch, "E367", {"start": v(-0.79, 0.84) * mm, "end": v(-0.6, 0.66) * mm});
            skLineSegment(sketch, "E368", {"start": v(-0.6, 0.66) * mm, "end": v(-0.64, 0.62) * mm});
            skLineSegment(sketch, "E369", {"start": v(-0.64, 0.62) * mm, "end": v(-0.66, 0.64) * mm});
            skLineSegment(sketch, "E370", {"start": v(-0.66, 0.64) * mm, "end": v(-0.66, 0.6) * mm});
            skLineSegment(sketch, "E371", {"start": v(-0.66, 0.6) * mm, "end": v(-0.67, 0.57) * mm});
            skLineSegment(sketch, "E372", {"start": v(-0.67, 0.57) * mm, "end": v(-0.7, 0.55) * mm});
            skLineSegment(sketch, "E373", {"start": v(-0.7, 0.55) * mm, "end": v(-0.73, 0.54) * mm});
            skLineSegment(sketch, "E374", {"start": v(-0.73, 0.54) * mm, "end": v(-0.77, 0.55) * mm});
            skLineSegment(sketch, "E375", {"start": v(-0.77, 0.55) * mm, "end": v(-0.8, 0.57) * mm});
            skLineSegment(sketch, "E376", {"start": v(-0.8, 0.57) * mm, "end": v(-0.83, 0.6) * mm});
            skLineSegment(sketch, "E377", {"start": v(-0.83, 0.6) * mm, "end": v(-0.84, 0.64) * mm});
            skLineSegment(sketch, "E378", {"start": v(-0.84, 0.64) * mm, "end": v(-0.84, 0.67) * mm});
            skLineSegment(sketch, "E379", {"start": v(-0.84, 0.67) * mm, "end": v(-0.82, 0.7) * mm});
            skLineSegment(sketch, "E380", {"start": v(-0.82, 0.7) * mm, "end": v(-0.8, 0.72) * mm});
            skLineSegment(sketch, "E381", {"start": v(-0.8, 0.72) * mm, "end": v(-0.76, 0.73) * mm});
            skLineSegment(sketch, "E382", {"start": v(-0.7, 0.61) * mm, "end": v(-0.68, 0.65) * mm});
            skLineSegment(sketch, "E383", {"start": v(-0.68, 0.65) * mm, "end": v(-0.7, 0.68) * mm});
            skLineSegment(sketch, "E384", {"start": v(-0.7, 0.68) * mm, "end": v(-0.74, 0.7) * mm});
            skLineSegment(sketch, "E385", {"start": v(-0.74, 0.7) * mm, "end": v(-0.77, 0.69) * mm});
            skLineSegment(sketch, "E386", {"start": v(-0.77, 0.69) * mm, "end": v(-0.78, 0.66) * mm});
            skLineSegment(sketch, "E387", {"start": v(-0.78, 0.66) * mm, "end": v(-0.76, 0.62) * mm});
            skLineSegment(sketch, "E388", {"start": v(-0.76, 0.62) * mm, "end": v(-0.72, 0.6) * mm});
            skLineSegment(sketch, "E389", {"start": v(-0.72, 0.6) * mm, "end": v(-0.7, 0.61) * mm});
            skLineSegment(sketch, "E390", {"start": v(-0.52, 0.82) * mm, "end": v(-0.54, 0.8) * mm});
            skLineSegment(sketch, "E391", {"start": v(-0.54, 0.8) * mm, "end": v(-0.54, 0.78) * mm});
            skLineSegment(sketch, "E392", {"start": v(-0.54, 0.78) * mm, "end": v(-0.52, 0.76) * mm});
            skLineSegment(sketch, "E393", {"start": v(-0.52, 0.76) * mm, "end": v(-0.5, 0.77) * mm});
            skLineSegment(sketch, "E394", {"start": v(-0.5, 0.77) * mm, "end": v(-0.48, 0.8) * mm});
            skLineSegment(sketch, "E395", {"start": v(-0.48, 0.8) * mm, "end": v(-0.49, 0.83) * mm});
            skLineSegment(sketch, "E396", {"start": v(-0.49, 0.83) * mm, "end": v(-0.5, 0.83) * mm});
            skLineSegment(sketch, "E397", {"start": v(-0.5, 0.83) * mm, "end": v(-0.52, 0.82) * mm});
            skLineSegment(sketch, "E398", {"start": v(-0.45, 0.89) * mm, "end": v(-0.4, 0.8) * mm});
            skLineSegment(sketch, "E399", {"start": v(-0.4, 0.8) * mm, "end": v(-0.45, 0.76) * mm});
            skLineSegment(sketch, "E400", {"start": v(-0.45, 0.76) * mm, "end": v(-0.46, 0.79) * mm});
            skLineSegment(sketch, "E401", {"start": v(-0.46, 0.79) * mm, "end": v(-0.47, 0.75) * mm});
            skLineSegment(sketch, "E402", {"start": v(-0.47, 0.75) * mm, "end": v(-0.5, 0.72) * mm});
            skLineSegment(sketch, "E403", {"start": v(-0.5, 0.72) * mm, "end": v(-0.55, 0.71) * mm});
            skLineSegment(sketch, "E404", {"start": v(-0.55, 0.71) * mm, "end": v(-0.57, 0.72) * mm});
            skLineSegment(sketch, "E405", {"start": v(-0.57, 0.72) * mm, "end": v(-0.6, 0.74) * mm});
            skLineSegment(sketch, "E406", {"start": v(-0.6, 0.74) * mm, "end": v(-0.6, 0.77) * mm});
            skLineSegment(sketch, "E407", {"start": v(-0.6, 0.77) * mm, "end": v(-0.6, 0.8) * mm});
            skLineSegment(sketch, "E408", {"start": v(-0.6, 0.8) * mm, "end": v(-0.58, 0.82) * mm});
            skLineSegment(sketch, "E409", {"start": v(-0.58, 0.82) * mm, "end": v(-0.54, 0.85) * mm});
            skLineSegment(sketch, "E410", {"start": v(-0.54, 0.85) * mm, "end": v(-0.51, 0.87) * mm});
            skLineSegment(sketch, "E411", {"start": v(-0.51, 0.87) * mm, "end": v(-0.52, 0.87) * mm});
            skLineSegment(sketch, "E412", {"start": v(-0.52, 0.87) * mm, "end": v(-0.54, 0.88) * mm});
            skLineSegment(sketch, "E413", {"start": v(-0.54, 0.88) * mm, "end": v(-0.57, 0.87) * mm});
            skLineSegment(sketch, "E414", {"start": v(-0.57, 0.87) * mm, "end": v(-0.6, 0.85) * mm});
            skLineSegment(sketch, "E415", {"start": v(-0.6, 0.85) * mm, "end": v(-0.62, 0.82) * mm});
            skLineSegment(sketch, "E416", {"start": v(-0.62, 0.82) * mm, "end": v(-0.64, 0.86) * mm});
            skLineSegment(sketch, "E417", {"start": v(-0.64, 0.86) * mm, "end": v(-0.61, 0.89) * mm});
            skLineSegment(sketch, "E418", {"start": v(-0.61, 0.89) * mm, "end": v(-0.58, 0.9) * mm});
            skLineSegment(sketch, "E419", {"start": v(-0.58, 0.9) * mm, "end": v(-0.54, 0.93) * mm});
            skLineSegment(sketch, "E420", {"start": v(-0.54, 0.93) * mm, "end": v(-0.5, 0.93) * mm});
            skLineSegment(sketch, "E421", {"start": v(-0.5, 0.93) * mm, "end": v(-0.48, 0.92) * mm});
            skLineSegment(sketch, "E422", {"start": v(-0.48, 0.92) * mm, "end": v(-0.45, 0.89) * mm});
            skLineSegment(sketch, "E423", {"start": v(-0.26, 1.04) * mm, "end": v(-0.24, 1) * mm});
            skLineSegment(sketch, "E424", {"start": v(-0.24, 1) * mm, "end": v(-0.28, 1) * mm});
            skLineSegment(sketch, "E425", {"start": v(-0.28, 1) * mm, "end": v(-0.32, 0.99) * mm});
            skLineSegment(sketch, "E426", {"start": v(-0.32, 0.99) * mm, "end": v(-0.34, 0.97) * mm});
            skLineSegment(sketch, "E427", {"start": v(-0.34, 0.97) * mm, "end": v(-0.34, 0.96) * mm});
            skLineSegment(sketch, "E428", {"start": v(-0.34, 0.96) * mm, "end": v(-0.33, 0.95) * mm});
            skLineSegment(sketch, "E429", {"start": v(-0.33, 0.95) * mm, "end": v(-0.31, 0.95) * mm});
            skLineSegment(sketch, "E430", {"start": v(-0.31, 0.95) * mm, "end": v(-0.3, 0.95) * mm});
            skLineSegment(sketch, "E431", {"start": v(-0.3, 0.95) * mm, "end": v(-0.26, 0.96) * mm});
            skLineSegment(sketch, "E432", {"start": v(-0.26, 0.96) * mm, "end": v(-0.23, 0.95) * mm});
            skLineSegment(sketch, "E433", {"start": v(-0.23, 0.95) * mm, "end": v(-0.22, 0.94) * mm});
            skLineSegment(sketch, "E434", {"start": v(-0.22, 0.94) * mm, "end": v(-0.2, 0.92) * mm});
            skLineSegment(sketch, "E435", {"start": v(-0.2, 0.92) * mm, "end": v(-0.2, 0.9) * mm});
            skLineSegment(sketch, "E436", {"start": v(-0.2, 0.9) * mm, "end": v(-0.21, 0.87) * mm});
            skLineSegment(sketch, "E437", {"start": v(-0.21, 0.87) * mm, "end": v(-0.24, 0.85) * mm});
            skLineSegment(sketch, "E438", {"start": v(-0.24, 0.85) * mm, "end": v(-0.27, 0.83) * mm});
            skLineSegment(sketch, "E439", {"start": v(-0.27, 0.83) * mm, "end": v(-0.31, 0.82) * mm});
            skLineSegment(sketch, "E440", {"start": v(-0.31, 0.82) * mm, "end": v(-0.35, 0.82) * mm});
            skLineSegment(sketch, "E441", {"start": v(-0.35, 0.82) * mm, "end": v(-0.37, 0.86) * mm});
            skLineSegment(sketch, "E442", {"start": v(-0.37, 0.86) * mm, "end": v(-0.33, 0.86) * mm});
            skLineSegment(sketch, "E443", {"start": v(-0.33, 0.86) * mm, "end": v(-0.29, 0.87) * mm});
            skLineSegment(sketch, "E444", {"start": v(-0.29, 0.87) * mm, "end": v(-0.26, 0.88) * mm});
            skLineSegment(sketch, "E445", {"start": v(-0.26, 0.88) * mm, "end": v(-0.26, 0.9) * mm});
            skLineSegment(sketch, "E446", {"start": v(-0.26, 0.9) * mm, "end": v(-0.27, 0.9) * mm});
            skLineSegment(sketch, "E447", {"start": v(-0.27, 0.9) * mm, "end": v(-0.3, 0.9) * mm});
            skLineSegment(sketch, "E448", {"start": v(-0.3, 0.9) * mm, "end": v(-0.3, 0.9) * mm});
            skLineSegment(sketch, "E449", {"start": v(-0.3, 0.9) * mm, "end": v(-0.34, 0.9) * mm});
            skLineSegment(sketch, "E450", {"start": v(-0.34, 0.9) * mm, "end": v(-0.37, 0.9) * mm});
            skLineSegment(sketch, "E451", {"start": v(-0.37, 0.9) * mm, "end": v(-0.38, 0.92) * mm});
            skLineSegment(sketch, "E452", {"start": v(-0.38, 0.92) * mm, "end": v(-0.4, 0.94) * mm});
            skLineSegment(sketch, "E453", {"start": v(-0.4, 0.94) * mm, "end": v(-0.4, 0.97) * mm});
            skLineSegment(sketch, "E454", {"start": v(-0.4, 0.97) * mm, "end": v(-0.39, 1) * mm});
            skLineSegment(sketch, "E455", {"start": v(-0.39, 1) * mm, "end": v(-0.37, 1) * mm});
            skLineSegment(sketch, "E456", {"start": v(-0.37, 1) * mm, "end": v(-0.33, 1.02) * mm});
            skLineSegment(sketch, "E457", {"start": v(-0.33, 1.02) * mm, "end": v(-0.3, 1.03) * mm});
            skLineSegment(sketch, "E458", {"start": v(-0.3, 1.03) * mm, "end": v(-0.26, 1.04) * mm});
            skLineSegment(sketch, "E459", {"start": v(0.18, 1.11) * mm, "end": v(0.18, 1.06) * mm});
            skLineSegment(sketch, "E460", {"start": v(0.18, 1.06) * mm, "end": v(0.14, 1.08) * mm});
            skLineSegment(sketch, "E461", {"start": v(0.14, 1.08) * mm, "end": v(0.1, 1.08) * mm});
            skLineSegment(sketch, "E462", {"start": v(0.1, 1.08) * mm, "end": v(0.06, 1.08) * mm});
            skLineSegment(sketch, "E463", {"start": v(0.06, 1.08) * mm, "end": v(0.05, 1.06) * mm});
            skLineSegment(sketch, "E464", {"start": v(0.05, 1.06) * mm, "end": v(0.06, 1.05) * mm});
            skLineSegment(sketch, "E465", {"start": v(0.06, 1.05) * mm, "end": v(0.08, 1.03) * mm});
            skLineSegment(sketch, "E466", {"start": v(0.08, 1.03) * mm, "end": v(0.11, 1.03) * mm});
            skLineSegment(sketch, "E467", {"start": v(0.11, 1.03) * mm, "end": v(0.15, 1.01) * mm});
            skLineSegment(sketch, "E468", {"start": v(0.15, 1.01) * mm, "end": v(0.17, 1) * mm});
            skLineSegment(sketch, "E469", {"start": v(0.17, 1) * mm, "end": v(0.18, 0.97) * mm});
            skLineSegment(sketch, "E470", {"start": v(0.18, 0.97) * mm, "end": v(0.18, 0.94) * mm});
            skLineSegment(sketch, "E471", {"start": v(0.18, 0.94) * mm, "end": v(0.17, 0.9) * mm});
            skLineSegment(sketch, "E472", {"start": v(0.17, 0.9) * mm, "end": v(0.15, 0.88) * mm});
            skLineSegment(sketch, "E473", {"start": v(0.15, 0.88) * mm, "end": v(0.12, 0.87) * mm});
            skLineSegment(sketch, "E474", {"start": v(0.12, 0.87) * mm, "end": v(0.07, 0.87) * mm});
            skLineSegment(sketch, "E475", {"start": v(0.07, 0.87) * mm, "end": v(0.03, 0.88) * mm});
            skLineSegment(sketch, "E476", {"start": v(0.03, 0.88) * mm, "end": v(-0.02, 0.9) * mm});
            skLineSegment(sketch, "E477", {"start": v(-0.02, 0.9) * mm, "end": v(-0.02, 0.95) * mm});
            skLineSegment(sketch, "E478", {"start": v(-0.02, 0.95) * mm, "end": v(0.03, 0.93) * mm});
            skLineSegment(sketch, "E479", {"start": v(0.03, 0.93) * mm, "end": v(0.07, 0.92) * mm});
            skLineSegment(sketch, "E480", {"start": v(0.07, 0.92) * mm, "end": v(0.1, 0.92) * mm});
            skLineSegment(sketch, "E481", {"start": v(0.1, 0.92) * mm, "end": v(0.12, 0.94) * mm});
            skLineSegment(sketch, "E482", {"start": v(0.12, 0.94) * mm, "end": v(0.11, 0.96) * mm});
            skLineSegment(sketch, "E483", {"start": v(0.11, 0.96) * mm, "end": v(0.08, 0.97) * mm});
            skLineSegment(sketch, "E484", {"start": v(0.08, 0.97) * mm, "end": v(0.06, 0.98) * mm});
            skLineSegment(sketch, "E485", {"start": v(0.06, 0.98) * mm, "end": v(0.03, 1) * mm});
            skLineSegment(sketch, "E486", {"start": v(0.03, 1) * mm, "end": v(0, 1.01) * mm});
            skLineSegment(sketch, "E487", {"start": v(0, 1.01) * mm, "end": v(0, 1.04) * mm});
            skLineSegment(sketch, "E488", {"start": v(0, 1.04) * mm, "end": v(0, 1.06) * mm});
            skLineSegment(sketch, "E489", {"start": v(0, 1.06) * mm, "end": v(0, 1.1) * mm});
            skLineSegment(sketch, "E490", {"start": v(0, 1.1) * mm, "end": v(0.02, 1.12) * mm});
            skLineSegment(sketch, "E491", {"start": v(0.02, 1.12) * mm, "end": v(0.05, 1.13) * mm});
            skLineSegment(sketch, "E492", {"start": v(0.05, 1.13) * mm, "end": v(0.1, 1.13) * mm});
            skLineSegment(sketch, "E493", {"start": v(0.1, 1.13) * mm, "end": v(0.14, 1.13) * mm});
            skLineSegment(sketch, "E494", {"start": v(0.14, 1.13) * mm, "end": v(0.18, 1.11) * mm});
            skLineSegment(sketch, "E495", {"start": v(0.3, 0.85) * mm, "end": v(0.26, 0.76) * mm});
            skLineSegment(sketch, "E496", {"start": v(0.26, 0.76) * mm, "end": v(0.2, 0.78) * mm});
            skLineSegment(sketch, "E497", {"start": v(0.2, 0.78) * mm, "end": v(0.3, 1.03) * mm});
            skLineSegment(sketch, "E498", {"start": v(0.3, 1.03) * mm, "end": v(0.36, 1) * mm});
            skLineSegment(sketch, "E499", {"start": v(0.36, 1) * mm, "end": v(0.35, 0.98) * mm});
            skLineSegment(sketch, "E500", {"start": v(0.35, 0.98) * mm, "end": v(0.38, 1) * mm});
            skLineSegment(sketch, "E501", {"start": v(0.38, 1) * mm, "end": v(0.42, 0.99) * mm});
            skLineSegment(sketch, "E502", {"start": v(0.42, 0.99) * mm, "end": v(0.44, 0.97) * mm});
            skLineSegment(sketch, "E503", {"start": v(0.44, 0.97) * mm, "end": v(0.46, 0.94) * mm});
            skLineSegment(sketch, "E504", {"start": v(0.46, 0.94) * mm, "end": v(0.46, 0.9) * mm});
            skLineSegment(sketch, "E505", {"start": v(0.46, 0.9) * mm, "end": v(0.45, 0.86) * mm});
            skLineSegment(sketch, "E506", {"start": v(0.45, 0.86) * mm, "end": v(0.43, 0.83) * mm});
            skLineSegment(sketch, "E507", {"start": v(0.43, 0.83) * mm, "end": v(0.4, 0.8) * mm});
            skLineSegment(sketch, "E508", {"start": v(0.4, 0.8) * mm, "end": v(0.37, 0.8) * mm});
            skLineSegment(sketch, "E509", {"start": v(0.37, 0.8) * mm, "end": v(0.34, 0.8) * mm});
            skLineSegment(sketch, "E510", {"start": v(0.34, 0.8) * mm, "end": v(0.31, 0.82) * mm});
            skLineSegment(sketch, "E511", {"start": v(0.31, 0.82) * mm, "end": v(0.3, 0.85) * mm});
            skLineSegment(sketch, "E512", {"start": v(0.38, 0.95) * mm, "end": v(0.35, 0.95) * mm});
            skLineSegment(sketch, "E513", {"start": v(0.35, 0.95) * mm, "end": v(0.32, 0.92) * mm});
            skLineSegment(sketch, "E514", {"start": v(0.32, 0.92) * mm, "end": v(0.31, 0.87) * mm});
            skLineSegment(sketch, "E515", {"start": v(0.31, 0.87) * mm, "end": v(0.34, 0.85) * mm});
            skLineSegment(sketch, "E516", {"start": v(0.34, 0.85) * mm, "end": v(0.37, 0.85) * mm});
            skLineSegment(sketch, "E517", {"start": v(0.37, 0.85) * mm, "end": v(0.4, 0.89) * mm});
            skLineSegment(sketch, "E518", {"start": v(0.4, 0.89) * mm, "end": v(0.4, 0.93) * mm});
            skLineSegment(sketch, "E519", {"start": v(0.4, 0.93) * mm, "end": v(0.38, 0.95) * mm});
            skLineSegment(sketch, "E520", {"start": v(0.56, 0.9) * mm, "end": v(0.61, 0.87) * mm});
            skLineSegment(sketch, "E521", {"start": v(0.61, 0.87) * mm, "end": v(0.5, 0.71) * mm});
            skLineSegment(sketch, "E522", {"start": v(0.5, 0.71) * mm, "end": v(0.46, 0.75) * mm});
            skLineSegment(sketch, "E523", {"start": v(0.46, 0.75) * mm, "end": v(0.56, 0.9) * mm});
            skLineSegment(sketch, "E524", {"start": v(0.6, 0.97) * mm, "end": v(0.65, 0.93) * mm});
            skLineSegment(sketch, "E525", {"start": v(0.65, 0.93) * mm, "end": v(0.63, 0.9) * mm});
            skLineSegment(sketch, "E526", {"start": v(0.63, 0.9) * mm, "end": v(0.57, 0.93) * mm});
            skLineSegment(sketch, "E527", {"start": v(0.57, 0.93) * mm, "end": v(0.6, 0.97) * mm});
            skLineSegment(sketch, "E528", {"start": v(0.76, 0.61) * mm, "end": v(0.74, 0.6) * mm});
            skLineSegment(sketch, "E529", {"start": v(0.74, 0.6) * mm, "end": v(0.64, 0.7) * mm});
            skLineSegment(sketch, "E530", {"start": v(0.64, 0.7) * mm, "end": v(0.63, 0.67) * mm});
            skLineSegment(sketch, "E531", {"start": v(0.63, 0.67) * mm, "end": v(0.65, 0.63) * mm});
            skLineSegment(sketch, "E532", {"start": v(0.65, 0.63) * mm, "end": v(0.68, 0.6) * mm});
            skLineSegment(sketch, "E533", {"start": v(0.68, 0.6) * mm, "end": v(0.72, 0.6) * mm});
            skLineSegment(sketch, "E534", {"start": v(0.72, 0.6) * mm, "end": v(0.7, 0.56) * mm});
            skLineSegment(sketch, "E535", {"start": v(0.7, 0.56) * mm, "end": v(0.65, 0.58) * mm});
            skLineSegment(sketch, "E536", {"start": v(0.65, 0.58) * mm, "end": v(0.62, 0.6) * mm});
            skLineSegment(sketch, "E537", {"start": v(0.62, 0.6) * mm, "end": v(0.6, 0.65) * mm});
            skLineSegment(sketch, "E538", {"start": v(0.6, 0.65) * mm, "end": v(0.58, 0.68) * mm});
            skLineSegment(sketch, "E539", {"start": v(0.58, 0.68) * mm, "end": v(0.59, 0.72) * mm});
            skLineSegment(sketch, "E540", {"start": v(0.59, 0.72) * mm, "end": v(0.61, 0.76) * mm});
            skLineSegment(sketch, "E541", {"start": v(0.61, 0.76) * mm, "end": v(0.65, 0.78) * mm});
            skLineSegment(sketch, "E542", {"start": v(0.65, 0.78) * mm, "end": v(0.68, 0.79) * mm});
            skLineSegment(sketch, "E543", {"start": v(0.68, 0.79) * mm, "end": v(0.72, 0.78) * mm});
            skLineSegment(sketch, "E544", {"start": v(0.72, 0.78) * mm, "end": v(0.76, 0.75) * mm});
            skLineSegment(sketch, "E545", {"start": v(0.76, 0.75) * mm, "end": v(0.78, 0.72) * mm});
            skLineSegment(sketch, "E546", {"start": v(0.78, 0.72) * mm, "end": v(0.79, 0.68) * mm});
            skLineSegment(sketch, "E547", {"start": v(0.79, 0.68) * mm, "end": v(0.78, 0.65) * mm});
            skLineSegment(sketch, "E548", {"start": v(0.78, 0.65) * mm, "end": v(0.76, 0.61) * mm});
            skLineSegment(sketch, "E549", {"start": v(0.73, 0.67) * mm, "end": v(0.74, 0.7) * mm});
            skLineSegment(sketch, "E550", {"start": v(0.74, 0.7) * mm, "end": v(0.73, 0.72) * mm});
            skLineSegment(sketch, "E551", {"start": v(0.73, 0.72) * mm, "end": v(0.7, 0.74) * mm});
            skLineSegment(sketch, "E552", {"start": v(0.7, 0.74) * mm, "end": v(0.67, 0.73) * mm});
            skLineSegment(sketch, "E553", {"start": v(0.67, 0.73) * mm, "end": v(0.73, 0.67) * mm});
            skLineSegment(sketch, "E554", {"start": v(0.93, 0.65) * mm, "end": v(0.97, 0.6) * mm});
            skLineSegment(sketch, "E555", {"start": v(0.97, 0.6) * mm, "end": v(0.75, 0.45) * mm});
            skLineSegment(sketch, "E556", {"start": v(0.75, 0.45) * mm, "end": v(0.71, 0.5) * mm});
            skLineSegment(sketch, "E557", {"start": v(0.71, 0.5) * mm, "end": v(0.93, 0.65) * mm});
            skLineSegment(sketch, "E558", {"start": v(1.02, 0.49) * mm, "end": v(1.04, 0.43) * mm});
            skLineSegment(sketch, "E559", {"start": v(1.04, 0.43) * mm, "end": v(0.95, 0.4) * mm});
            skLineSegment(sketch, "E560", {"start": v(0.95, 0.4) * mm, "end": v(0.88, 0.37) * mm});
            skLineSegment(sketch, "E561", {"start": v(0.88, 0.37) * mm, "end": v(0.86, 0.41) * mm});
            skLineSegment(sketch, "E562", {"start": v(0.86, 0.41) * mm, "end": v(0.93, 0.45) * mm});
            skLineSegment(sketch, "E563", {"start": v(0.93, 0.45) * mm, "end": v(1.02, 0.49) * mm});
            skLineSegment(sketch, "E564", {"start": v(0.84, 0.4) * mm, "end": v(0.86, 0.35) * mm});
            skLineSegment(sketch, "E565", {"start": v(0.86, 0.35) * mm, "end": v(0.8, 0.33) * mm});
            skLineSegment(sketch, "E566", {"start": v(0.8, 0.33) * mm, "end": v(0.78, 0.38) * mm});
            skLineSegment(sketch, "E567", {"start": v(0.78, 0.38) * mm, "end": v(0.84, 0.4) * mm});
            skCircle(sketch, "E568", {"center": v(0, 0) * mm, "radius": 1.25 * mm});
            skCircle(sketch, "E569", {"center": v(0, 0) * mm, "radius": 0.5 * mm});
            skCircle(sketch, "E570", {"center": v(0, 0) * mm, "radius": 1.2 * mm});
            skCircle(sketch, "E571", {"center": v(0, 0) * mm, "radius": 0.55 * mm});
            skSolve(sketch);
        }
        {
            var Q0;
            Q0=makeQuery(id+"F0.imprint","IMPRINT",FACE,{"disambiguationData":[TD([[makeQuery(id+"F0.imprint","IMPRINT",EDGE,{"derivedFrom":sQuery(id+"F0.wireOp",EDGE,"E171")}),-1.0]])]});
            var Q1;
            Q1=makeQuery(id+"F0.imprint","IMPRINT",FACE,{"disambiguationData":[TD([[makeQuery(id+"F0.imprint","IMPRINT",EDGE,{"derivedFrom":sQuery(id+"F0.wireOp",EDGE,"E365")}),-1.0]])]});
            var Q2;
            Q2=makeQuery(id+"F0.imprint","IMPRINT",FACE,{"disambiguationData":[TD([[makeQuery(id+"F0.imprint","IMPRINT",EDGE,{"derivedFrom":sQuery(id+"F0.wireOp",EDGE,"E558")}),-1.0]])]});
            var Q3;
            Q3=makeQuery(id+"F0.imprint","IMPRINT",FACE,{"disambiguationData":[TD([[makeQuery(id+"F0.imprint","IMPRINT",EDGE,{"derivedFrom":sQuery(id+"F0.wireOp",EDGE,"E390")}),-1.0]])]});
            var Q4;
            Q4=makeQuery(id+"F0.imprint","IMPRINT",FACE,{"disambiguationData":[TD([[makeQuery(id+"F0.imprint","IMPRINT",EDGE,{"derivedFrom":sQuery(id+"F0.wireOp",EDGE,"E568")}),1.0]])]});
            var Q5;
            {var subQ5=sQuery(id+"F0.wireOp",EDGE,"E498");Q5=makeQuery(id+"F0.imprint","IMPRINT",FACE,{"disambiguationData":[TD([[makeQuery(id+"F0.imprint","IMPRINT",EDGE,{"derivedFrom":subQ5}),-1.0]])]});}
            var Q6;
            {var subQ85=sQuery(id+"F0.wireOp",EDGE,"E3");Q6=makeQuery(id+"F0.imprint","IMPRINT",FACE,{"disambiguationData":[TD([[makeQuery(id+"F0.imprint","IMPRINT",EDGE,{"derivedFrom":subQ85}),-1.0]])]});}
            var Q7;
            {var subQ23=sQuery(id+"F0.wireOp",EDGE,"E3");Q7=makeQuery(id+"F0.imprint","IMPRINT",FACE,{"disambiguationData":[TD([[makeQuery(id+"F0.imprint","IMPRINT",EDGE,{"derivedFrom":subQ23}),1.0]])]});}
            var Q8;
            {var subQ5=sQuery(id+"F0.wireOp",EDGE,"E496");Q8=makeQuery(id+"F0.imprint","IMPRINT",FACE,{"disambiguationData":[TD([[makeQuery(id+"F0.imprint","IMPRINT",EDGE,{"derivedFrom":subQ5}),-1.0]])]});}
            var Q9;
            Q9=makeQuery(id+"F0.imprint","IMPRINT",FACE,{"disambiguationData":[TD([[makeQuery(id+"F0.imprint","IMPRINT",EDGE,{"derivedFrom":sQuery(id+"F0.wireOp",EDGE,"E520")}),-1.0]])]});
            var Q10;
            Q10=makeQuery(id+"F0.imprint","IMPRINT",FACE,{"disambiguationData":[TD([[makeQuery(id+"F0.imprint","IMPRINT",EDGE,{"derivedFrom":sQuery(id+"F0.wireOp",EDGE,"E554")}),-1.0]])]});
            var Q11;
            Q11=makeQuery(id+"F0.imprint","IMPRINT",FACE,{"disambiguationData":[TD([[makeQuery(id+"F0.imprint","IMPRINT",EDGE,{"derivedFrom":sQuery(id+"F0.wireOp",EDGE,"E91")}),-1.0]])]});
            var Q12;
            Q12=makeQuery(id+"F0.imprint","IMPRINT",FACE,{"disambiguationData":[TD([[makeQuery(id+"F0.imprint","IMPRINT",EDGE,{"derivedFrom":sQuery(id+"F0.wireOp",EDGE,"E112")}),1.0]])]});
            var Q13;
            Q13=makeQuery(id+"F0.imprint","IMPRINT",FACE,{"disambiguationData":[TD([[makeQuery(id+"F0.imprint","IMPRINT",EDGE,{"derivedFrom":sQuery(id+"F0.wireOp",EDGE,"E160")}),-1.0]])]});
            var Q14;
            Q14=makeQuery(id+"F0.imprint","IMPRINT",FACE,{"disambiguationData":[TD([[makeQuery(id+"F0.imprint","IMPRINT",EDGE,{"derivedFrom":sQuery(id+"F0.wireOp",EDGE,"E197")}),-1.0]])]});
            var Q15;
            Q15=makeQuery(id+"F0.imprint","IMPRINT",FACE,{"disambiguationData":[TD([[makeQuery(id+"F0.imprint","IMPRINT",EDGE,{"derivedFrom":sQuery(id+"F0.wireOp",EDGE,"E218")}),-1.0]])]});
            var Q16;
            Q16=makeQuery(id+"F0.imprint","IMPRINT",FACE,{"disambiguationData":[TD([[makeQuery(id+"F0.imprint","IMPRINT",EDGE,{"derivedFrom":sQuery(id+"F0.wireOp",EDGE,"E265")}),-1.0]])]});
            var Q17;
            Q17=makeQuery(id+"F0.imprint","IMPRINT",FACE,{"disambiguationData":[TD([[makeQuery(id+"F0.imprint","IMPRINT",EDGE,{"derivedFrom":sQuery(id+"F0.wireOp",EDGE,"E345")}),-1.0]])]});
            var Q18;
            Q18=makeQuery(id+"F0.imprint","IMPRINT",FACE,{"disambiguationData":[TD([[makeQuery(id+"F0.imprint","IMPRINT",EDGE,{"derivedFrom":sQuery(id+"F0.wireOp",EDGE,"E528")}),-1.0]])]});
            var Q19;
            Q19=makeQuery(id+"F0.imprint","IMPRINT",FACE,{"disambiguationData":[TD([[makeQuery(id+"F0.imprint","IMPRINT",EDGE,{"derivedFrom":sQuery(id+"F0.wireOp",EDGE,"E309")}),-1.0]])]});
            var Q20;
            Q20=makeQuery(id+"F0.imprint","IMPRINT",FACE,{"disambiguationData":[TD([[makeQuery(id+"F0.imprint","IMPRINT",EDGE,{"derivedFrom":sQuery(id+"F0.wireOp",EDGE,"E239")}),-1.0]])]});
            var Q21;
            Q21=makeQuery(id+"F0.imprint","IMPRINT",FACE,{"disambiguationData":[TD([[makeQuery(id+"F0.imprint","IMPRINT",EDGE,{"derivedFrom":sQuery(id+"F0.wireOp",EDGE,"E112")}),-1.0]])]});
            var Q22;
            Q22=makeQuery(id+"F0.imprint","IMPRINT",FACE,{"disambiguationData":[TD([[makeQuery(id+"F0.imprint","IMPRINT",EDGE,{"derivedFrom":sQuery(id+"F0.wireOp",EDGE,"E273")}),-1.0]])]});
            var Q23;
            Q23=makeQuery(id+"F0.imprint","IMPRINT",FACE,{"disambiguationData":[TD([[makeQuery(id+"F0.imprint","IMPRINT",EDGE,{"derivedFrom":sQuery(id+"F0.wireOp",EDGE,"E564")}),-1.0]])]});
            var Q24;
            Q24=makeQuery(id+"F0.imprint","IMPRINT",FACE,{"disambiguationData":[TD([[makeQuery(id+"F0.imprint","IMPRINT",EDGE,{"derivedFrom":sQuery(id+"F0.wireOp",EDGE,"E423")}),-1.0]])]});
            var Q25;
            Q25=makeQuery(id+"F0.imprint","IMPRINT",FACE,{"disambiguationData":[TD([[makeQuery(id+"F0.imprint","IMPRINT",EDGE,{"derivedFrom":sQuery(id+"F0.wireOp",EDGE,"E32")}),-1.0]])]});
            var Q26;
            Q26=makeQuery(id+"F0.imprint","IMPRINT",FACE,{"disambiguationData":[TD([[makeQuery(id+"F0.imprint","IMPRINT",EDGE,{"derivedFrom":sQuery(id+"F0.wireOp",EDGE,"E459")}),-1.0]])]});
            var Q27;
            Q27=makeQuery(id+"F0.imprint","IMPRINT",FACE,{"disambiguationData":[TD([[makeQuery(id+"F0.imprint","IMPRINT",EDGE,{"derivedFrom":sQuery(id+"F0.wireOp",EDGE,"E68")}),-1.0]])]});
            var Q28;
            {var subQ5=sQuery(id+"F0.wireOp",EDGE,"E511");Q28=makeQuery(id+"F0.imprint","IMPRINT",FACE,{"disambiguationData":[TD([[makeQuery(id+"F0.imprint","IMPRINT",EDGE,{"derivedFrom":subQ5}),1.0]])]});}
            var Q29;
            Q29=makeQuery(id+"F0.imprint","IMPRINT",FACE,{"disambiguationData":[TD([[makeQuery(id+"F0.imprint","IMPRINT",EDGE,{"derivedFrom":sQuery(id+"F0.wireOp",EDGE,"E136")}),-1.0]])]});
            var Q30;
            Q30=makeQuery(id+"F0.imprint","IMPRINT",FACE,{"disambiguationData":[TD([[makeQuery(id+"F0.imprint","IMPRINT",EDGE,{"derivedFrom":sQuery(id+"F0.wireOp",EDGE,"E524")}),-1.0]])]});
            var Q31;
            Q31=makeQuery(id+"F0.imprint","IMPRINT",FACE,{"disambiguationData":[TD([[makeQuery(id+"F0.imprint","IMPRINT",EDGE,{"derivedFrom":sQuery(id+"F0.wireOp",EDGE,"E260")}),1.0]])]});
            var Q32;
            Q32=makeQuery(id+"F0.imprint","IMPRINT",FACE,{"disambiguationData":[TD([[makeQuery(id+"F0.imprint","IMPRINT",EDGE,{"derivedFrom":sQuery(id+"F0.wireOp",EDGE,"E269")}),-1.0]])]});
            var Q33;
            Q33=makeQuery(id+"F0.imprint","IMPRINT",FACE,{"disambiguationData":[TD([[makeQuery(id+"F0.imprint","IMPRINT",EDGE,{"derivedFrom":sQuery(id+"F0.wireOp",EDGE,"E382")}),1.0]])]});
            var Q34;
            Q34=makeQuery(id+"F0.imprint","IMPRINT",FACE,{"disambiguationData":[TD([[makeQuery(id+"F0.imprint","IMPRINT",EDGE,{"derivedFrom":sQuery(id+"F0.wireOp",EDGE,"E512")}),1.0]])]});
            var Q35;
            Q35=makeQuery(id+"F0.imprint","IMPRINT",FACE,{"disambiguationData":[TD([[makeQuery(id+"F0.imprint","IMPRINT",EDGE,{"derivedFrom":sQuery(id+"F0.wireOp",EDGE,"E549")}),1.0]])]});
            var Q36;
            Q36=makeQuery(id+"F0.imprint","IMPRINT",FACE,{"disambiguationData":[TD([[makeQuery(id+"F0.imprint","IMPRINT",EDGE,{"derivedFrom":sQuery(id+"F0.wireOp",EDGE,"E192")}),1.0]])]});
            var Q37;
            Q37=makeQuery(id+"F0.imprint","IMPRINT",FACE,{"disambiguationData":[TD([[makeQuery(id+"F0.imprint","IMPRINT",EDGE,{"derivedFrom":sQuery(id+"F0.wireOp",EDGE,"E390")}),1.0]])]});
            var Q38;
            {var subQ0=sQuery(id+"F0.wireOp",EDGE,"E289");var subQ1=sQuery(id+"F0.wireOp",EDGE,"E15");var subQ2=makeQuery(id+"F0.imprint","INTERSECT",VERTEX,{"derivedFrom":[subQ1,subQ0]});Q38=makeQuery(id+"F0.imprint","IMPRINT",FACE,{"disambiguationData":[TD([[makeQuery(id+"F0.imprint","IMPRINT",EDGE,{"disambiguationData":[TD([[subQ2,-1.0]])],"derivedFrom":subQ1}),-1.0]])]});}
            var Q39;
            {var subQ0=sQuery(id+"F0.wireOp",EDGE,"E325");var subQ1=sQuery(id+"F0.wireOp",EDGE,"E16");var subQ2=makeQuery(id+"F0.imprint","INTERSECT",VERTEX,{"derivedFrom":[subQ1,subQ0]});Q39=makeQuery(id+"F0.imprint","IMPRINT",FACE,{"disambiguationData":[TD([[makeQuery(id+"F0.imprint","IMPRINT",EDGE,{"disambiguationData":[TD([[subQ2,-1.0]])],"derivedFrom":subQ1}),-1.0]])]});}
            var Q40;
            {var subQ0=sQuery(id+"F0.wireOp",EDGE,"E372");var subQ1=sQuery(id+"F0.wireOp",EDGE,"E19");var subQ2=makeQuery(id+"F0.imprint","INTERSECT",VERTEX,{"derivedFrom":[subQ1,subQ0]});Q40=makeQuery(id+"F0.imprint","IMPRINT",FACE,{"disambiguationData":[TD([[makeQuery(id+"F0.imprint","IMPRINT",EDGE,{"disambiguationData":[TD([[subQ2,-1.0]])],"derivedFrom":subQ1}),-1.0]])]});}
            var Q41;
            {var subQ0=sQuery(id+"F0.wireOp",EDGE,"E439");var subQ1=sQuery(id+"F0.wireOp",EDGE,"E22");var subQ2=makeQuery(id+"F0.imprint","INTERSECT",VERTEX,{"derivedFrom":[subQ1,subQ0]});Q41=makeQuery(id+"F0.imprint","IMPRINT",FACE,{"disambiguationData":[TD([[makeQuery(id+"F0.imprint","IMPRINT",EDGE,{"disambiguationData":[TD([[subQ2,-1.0]])],"derivedFrom":subQ1}),-1.0]])]});}
            var Q42;
            {var subQ0=sQuery(id+"F0.wireOp",EDGE,"E48");var subQ1=sQuery(id+"F0.wireOp",EDGE,"E0");var subQ2=makeQuery(id+"F0.imprint","INTERSECT",VERTEX,{"derivedFrom":[subQ1,subQ0]});Q42=makeQuery(id+"F0.imprint","IMPRINT",FACE,{"disambiguationData":[TD([[makeQuery(id+"F0.imprint","IMPRINT",EDGE,{"disambiguationData":[TD([[subQ2,-1.0]])],"derivedFrom":subQ1}),-1.0]])]});}
            var Q43;
            {var subQ0=sQuery(id+"F0.wireOp",EDGE,"E475");var subQ1=sQuery(id+"F0.wireOp",EDGE,"E24");var subQ2=makeQuery(id+"F0.imprint","INTERSECT",VERTEX,{"derivedFrom":[subQ1,subQ0]});Q43=makeQuery(id+"F0.imprint","IMPRINT",FACE,{"disambiguationData":[TD([[makeQuery(id+"F0.imprint","IMPRINT",EDGE,{"disambiguationData":[TD([[subQ2,-1.0]])],"derivedFrom":subQ1}),-1.0]])]});}
            var Q44;
            {var subQ0=sQuery(id+"F0.wireOp",EDGE,"E2");var subQ1=sQuery(id+"F0.wireOp",EDGE,"E1");var subQ2=makeQuery(id+"F0.imprint","INTERSECT",VERTEX,{"derivedFrom":[subQ1,subQ0]});Q44=makeQuery(id+"F0.imprint","IMPRINT",FACE,{"disambiguationData":[TD([[makeQuery(id+"F0.imprint","IMPRINT",EDGE,{"disambiguationData":[TD([[subQ2,1.0]])],"derivedFrom":subQ1}),-1.0]])]});}
            var Q45;
            {var subQ0=sQuery(id+"F0.wireOp",EDGE,"E128");var subQ1=sQuery(id+"F0.wireOp",EDGE,"E4");var subQ2=makeQuery(id+"F0.imprint","INTERSECT",VERTEX,{"derivedFrom":[subQ1,subQ0]});Q45=makeQuery(id+"F0.imprint","IMPRINT",FACE,{"disambiguationData":[TD([[makeQuery(id+"F0.imprint","IMPRINT",EDGE,{"disambiguationData":[TD([[subQ2,-1.0]])],"derivedFrom":subQ1}),-1.0]])]});}
            var Q46;
            {var subQ0=sQuery(id+"F0.wireOp",EDGE,"E26");var subQ1=sQuery(id+"F0.wireOp",EDGE,"E25");var subQ2=makeQuery(id+"F0.imprint","INTERSECT",VERTEX,{"derivedFrom":[subQ1,subQ0]});Q46=makeQuery(id+"F0.imprint","IMPRINT",FACE,{"disambiguationData":[TD([[makeQuery(id+"F0.imprint","IMPRINT",EDGE,{"disambiguationData":[TD([[subQ2,1.0]])],"derivedFrom":subQ1}),-1.0]])]});}
            var Q47;
            {var subQ0=sQuery(id+"F0.wireOp",EDGE,"E150");var subQ1=sQuery(id+"F0.wireOp",EDGE,"E6");var subQ2=makeQuery(id+"F0.imprint","INTERSECT",VERTEX,{"derivedFrom":[subQ1,subQ0]});Q47=makeQuery(id+"F0.imprint","IMPRINT",FACE,{"disambiguationData":[TD([[makeQuery(id+"F0.imprint","IMPRINT",EDGE,{"disambiguationData":[TD([[subQ2,-1.0]])],"derivedFrom":subQ1}),-1.0]])]});}
            var Q48;
            {var subQ0=sQuery(id+"F0.wireOp",EDGE,"E180");var subQ1=sQuery(id+"F0.wireOp",EDGE,"E8");var subQ2=makeQuery(id+"F0.imprint","INTERSECT",VERTEX,{"derivedFrom":[subQ1,subQ0]});Q48=makeQuery(id+"F0.imprint","IMPRINT",FACE,{"disambiguationData":[TD([[makeQuery(id+"F0.imprint","IMPRINT",EDGE,{"disambiguationData":[TD([[subQ2,-1.0]])],"derivedFrom":subQ1}),-1.0]])]});}
            var Q49;
            {var subQ0=sQuery(id+"F0.wireOp",EDGE,"E28");var subQ1=sQuery(id+"F0.wireOp",EDGE,"E27");var subQ2=makeQuery(id+"F0.imprint","INTERSECT",VERTEX,{"derivedFrom":[subQ1,subQ0]});Q49=makeQuery(id+"F0.imprint","IMPRINT",FACE,{"disambiguationData":[TD([[makeQuery(id+"F0.imprint","IMPRINT",EDGE,{"disambiguationData":[TD([[subQ2,1.0]])],"derivedFrom":subQ1}),-1.0]])]});}
            var Q50;
            {var subQ0=sQuery(id+"F0.wireOp",EDGE,"E248");var subQ1=sQuery(id+"F0.wireOp",EDGE,"E13");var subQ2=makeQuery(id+"F0.imprint","INTERSECT",VERTEX,{"derivedFrom":[subQ1,subQ0]});Q50=makeQuery(id+"F0.imprint","IMPRINT",FACE,{"disambiguationData":[TD([[makeQuery(id+"F0.imprint","IMPRINT",EDGE,{"disambiguationData":[TD([[subQ2,-1.0]])],"derivedFrom":subQ1}),-1.0]])]});}
            var Q51;
            {var subQ0=sQuery(id+"F0.wireOp",EDGE,"E27");var subQ1=sQuery(id+"F0.wireOp",EDGE,"E26");var subQ2=makeQuery(id+"F0.imprint","INTERSECT",VERTEX,{"derivedFrom":[subQ1,subQ0]});Q51=makeQuery(id+"F0.imprint","IMPRINT",FACE,{"disambiguationData":[TD([[makeQuery(id+"F0.imprint","IMPRINT",EDGE,{"disambiguationData":[TD([[subQ2,1.0]])],"derivedFrom":subQ1}),-1.0]])]});}
            var Q52;
            {var subQ0=sQuery(id+"F0.wireOp",EDGE,"E21");var subQ1=sQuery(id+"F0.wireOp",EDGE,"E20");var subQ2=makeQuery(id+"F0.imprint","INTERSECT",VERTEX,{"derivedFrom":[subQ1,subQ0]});Q52=makeQuery(id+"F0.imprint","IMPRINT",FACE,{"disambiguationData":[TD([[makeQuery(id+"F0.imprint","IMPRINT",EDGE,{"disambiguationData":[TD([[subQ2,1.0]])],"derivedFrom":subQ1}),-1.0]])]});}
            var Q53;
            Q53=makeQuery(id+"F0.imprint","IMPRINT",FACE,{"disambiguationData":[TD([[makeQuery(id+"F0.imprint","IMPRINT",EDGE,{"derivedFrom":sQuery(id+"F0.wireOp",EDGE,"E569")}),-1.0]])]});
            extrude(context, id + "F1", {"entities" : qUnion([Q0, Q1, Q2, Q3, Q4, Q5, Q6, Q7, Q8, Q9, Q10, Q11, Q12, Q13, Q14, Q15, Q16, Q17, Q18, Q19, Q20, Q21, Q22, Q23, Q24, Q25, Q26, Q27, Q28, Q29, Q30, Q31, Q32, Q33, Q34, Q35, Q36, Q37, Q38, Q39, Q40, Q41, Q42, Q43, Q44, Q45, Q46, Q47, Q48, Q49, Q50, Q51, Q52, Q53]), "oppositeDirection" : true, "depth" : 2 * mm});
        }
        {
            var Q0;
            Q0=makeQuery(id+"F0.imprint","IMPRINT",FACE,{"disambiguationData":[TD([[makeQuery(id+"F0.imprint","IMPRINT",EDGE,{"derivedFrom":sQuery(id+"F0.wireOp",EDGE,"E365")}),-1.0]])]});
            var Q1;
            Q1=makeQuery(id+"F0.imprint","IMPRINT",FACE,{"disambiguationData":[TD([[makeQuery(id+"F0.imprint","IMPRINT",EDGE,{"derivedFrom":sQuery(id+"F0.wireOp",EDGE,"E390")}),-1.0]])]});
            var Q2;
            Q2=makeQuery(id+"F0.imprint","IMPRINT",FACE,{"disambiguationData":[TD([[makeQuery(id+"F0.imprint","IMPRINT",EDGE,{"derivedFrom":sQuery(id+"F0.wireOp",EDGE,"E423")}),-1.0]])]});
            var Q3;
            Q3=makeQuery(id+"F0.imprint","IMPRINT",FACE,{"disambiguationData":[TD([[makeQuery(id+"F0.imprint","IMPRINT",EDGE,{"derivedFrom":sQuery(id+"F0.wireOp",EDGE,"E459")}),-1.0]])]});
            var Q4;
            {var subQ5=sQuery(id+"F0.wireOp",EDGE,"E498");Q4=makeQuery(id+"F0.imprint","IMPRINT",FACE,{"disambiguationData":[TD([[makeQuery(id+"F0.imprint","IMPRINT",EDGE,{"derivedFrom":subQ5}),-1.0]])]});}
            var Q5;
            {var subQ5=sQuery(id+"F0.wireOp",EDGE,"E496");Q5=makeQuery(id+"F0.imprint","IMPRINT",FACE,{"disambiguationData":[TD([[makeQuery(id+"F0.imprint","IMPRINT",EDGE,{"derivedFrom":subQ5}),-1.0]])]});}
            var Q6;
            Q6=makeQuery(id+"F0.imprint","IMPRINT",FACE,{"disambiguationData":[TD([[makeQuery(id+"F0.imprint","IMPRINT",EDGE,{"derivedFrom":sQuery(id+"F0.wireOp",EDGE,"E520")}),-1.0]])]});
            var Q7;
            Q7=makeQuery(id+"F0.imprint","IMPRINT",FACE,{"disambiguationData":[TD([[makeQuery(id+"F0.imprint","IMPRINT",EDGE,{"derivedFrom":sQuery(id+"F0.wireOp",EDGE,"E524")}),-1.0]])]});
            var Q8;
            Q8=makeQuery(id+"F0.imprint","IMPRINT",FACE,{"disambiguationData":[TD([[makeQuery(id+"F0.imprint","IMPRINT",EDGE,{"derivedFrom":sQuery(id+"F0.wireOp",EDGE,"E554")}),-1.0]])]});
            var Q9;
            Q9=makeQuery(id+"F0.imprint","IMPRINT",FACE,{"disambiguationData":[TD([[makeQuery(id+"F0.imprint","IMPRINT",EDGE,{"derivedFrom":sQuery(id+"F0.wireOp",EDGE,"E564")}),-1.0]])]});
            var Q10;
            Q10=makeQuery(id+"F0.imprint","IMPRINT",FACE,{"disambiguationData":[TD([[makeQuery(id+"F0.imprint","IMPRINT",EDGE,{"derivedFrom":sQuery(id+"F0.wireOp",EDGE,"E558")}),-1.0]])]});
            var Q11;
            Q11=makeQuery(id+"F0.imprint","IMPRINT",FACE,{"disambiguationData":[TD([[makeQuery(id+"F0.imprint","IMPRINT",EDGE,{"derivedFrom":sQuery(id+"F0.wireOp",EDGE,"E528")}),-1.0]])]});
            var Q12;
            Q12=makeQuery(id+"F0.imprint","IMPRINT",FACE,{"disambiguationData":[TD([[makeQuery(id+"F0.imprint","IMPRINT",EDGE,{"derivedFrom":sQuery(id+"F0.wireOp",EDGE,"E218")}),-1.0]])]});
            var Q13;
            Q13=makeQuery(id+"F0.imprint","IMPRINT",FACE,{"disambiguationData":[TD([[makeQuery(id+"F0.imprint","IMPRINT",EDGE,{"derivedFrom":sQuery(id+"F0.wireOp",EDGE,"E239")}),-1.0]])]});
            var Q14;
            Q14=makeQuery(id+"F0.imprint","IMPRINT",FACE,{"disambiguationData":[TD([[makeQuery(id+"F0.imprint","IMPRINT",EDGE,{"derivedFrom":sQuery(id+"F0.wireOp",EDGE,"E265")}),-1.0]])]});
            var Q15;
            Q15=makeQuery(id+"F0.imprint","IMPRINT",FACE,{"disambiguationData":[TD([[makeQuery(id+"F0.imprint","IMPRINT",EDGE,{"derivedFrom":sQuery(id+"F0.wireOp",EDGE,"E269")}),-1.0]])]});
            var Q16;
            Q16=makeQuery(id+"F0.imprint","IMPRINT",FACE,{"disambiguationData":[TD([[makeQuery(id+"F0.imprint","IMPRINT",EDGE,{"derivedFrom":sQuery(id+"F0.wireOp",EDGE,"E309")}),-1.0]])]});
            var Q17;
            Q17=makeQuery(id+"F0.imprint","IMPRINT",FACE,{"disambiguationData":[TD([[makeQuery(id+"F0.imprint","IMPRINT",EDGE,{"derivedFrom":sQuery(id+"F0.wireOp",EDGE,"E345")}),-1.0]])]});
            var Q18;
            Q18=makeQuery(id+"F0.imprint","IMPRINT",FACE,{"disambiguationData":[TD([[makeQuery(id+"F0.imprint","IMPRINT",EDGE,{"derivedFrom":sQuery(id+"F0.wireOp",EDGE,"E273")}),-1.0]])]});
            var Q19;
            Q19=makeQuery(id+"F0.imprint","IMPRINT",FACE,{"disambiguationData":[TD([[makeQuery(id+"F0.imprint","IMPRINT",EDGE,{"derivedFrom":sQuery(id+"F0.wireOp",EDGE,"E197")}),-1.0]])]});
            var Q20;
            Q20=makeQuery(id+"F0.imprint","IMPRINT",FACE,{"disambiguationData":[TD([[makeQuery(id+"F0.imprint","IMPRINT",EDGE,{"derivedFrom":sQuery(id+"F0.wireOp",EDGE,"E171")}),-1.0]])]});
            var Q21;
            Q21=makeQuery(id+"F0.imprint","IMPRINT",FACE,{"disambiguationData":[TD([[makeQuery(id+"F0.imprint","IMPRINT",EDGE,{"derivedFrom":sQuery(id+"F0.wireOp",EDGE,"E160")}),-1.0]])]});
            var Q22;
            Q22=makeQuery(id+"F0.imprint","IMPRINT",FACE,{"disambiguationData":[TD([[makeQuery(id+"F0.imprint","IMPRINT",EDGE,{"derivedFrom":sQuery(id+"F0.wireOp",EDGE,"E136")}),-1.0]])]});
            var Q23;
            Q23=makeQuery(id+"F0.imprint","IMPRINT",FACE,{"disambiguationData":[TD([[makeQuery(id+"F0.imprint","IMPRINT",EDGE,{"derivedFrom":sQuery(id+"F0.wireOp",EDGE,"E112")}),-1.0]])]});
            var Q24;
            Q24=makeQuery(id+"F0.imprint","IMPRINT",FACE,{"disambiguationData":[TD([[makeQuery(id+"F0.imprint","IMPRINT",EDGE,{"derivedFrom":sQuery(id+"F0.wireOp",EDGE,"E91")}),-1.0]])]});
            var Q25;
            Q25=makeQuery(id+"F0.imprint","IMPRINT",FACE,{"disambiguationData":[TD([[makeQuery(id+"F0.imprint","IMPRINT",EDGE,{"derivedFrom":sQuery(id+"F0.wireOp",EDGE,"E68")}),-1.0]])]});
            var Q26;
            Q26=makeQuery(id+"F0.imprint","IMPRINT",FACE,{"disambiguationData":[TD([[makeQuery(id+"F0.imprint","IMPRINT",EDGE,{"derivedFrom":sQuery(id+"F0.wireOp",EDGE,"E32")}),-1.0]])]});
            var Q27;
            Q27=makeQuery(id+"F0.imprint","IMPRINT",FACE,{"disambiguationData":[TD([[makeQuery(id+"F0.imprint","IMPRINT",EDGE,{"derivedFrom":sQuery(id+"F0.wireOp",EDGE,"E568")}),1.0]])]});
            var Q28;
            Q28=makeQuery(id+"F0.imprint","IMPRINT",FACE,{"disambiguationData":[TD([[makeQuery(id+"F0.imprint","IMPRINT",EDGE,{"derivedFrom":sQuery(id+"F0.wireOp",EDGE,"E569")}),-1.0]])]});
            extrude(context, id + "F2", {"entities" : qUnion([Q0, Q1, Q2, Q3, Q4, Q5, Q6, Q7, Q8, Q9, Q10, Q11, Q12, Q13, Q14, Q15, Q16, Q17, Q18, Q19, Q20, Q21, Q22, Q23, Q24, Q25, Q26, Q27, Q28]), "operationType" : NewBodyOperationType.ADD, "depth" : 0.5 * mm});
        }
        {
            var Q0;
            Q0=makeQuery(id+"F1.opExtrude","SWEPT_BODY",BODY,{"disambiguationData":[OSD([sQuery(id+"F0.wireOp",EDGE,"E568"),sQuery(id+"F0.wireOp",EDGE,"E569")])]});
            var Q1;
            Q1=sQuery(id+"F0.wireOp",VERTEX,"E569.center");
            transform(context, id + "F3", {"entities" : qUnion([Q0]), "transformType" : TransformType.SCALE_UNIFORMLY, "scale" : 25, "scalePoint" : qUnion([Q1]), "makeCopy" : false});
        }
    });
